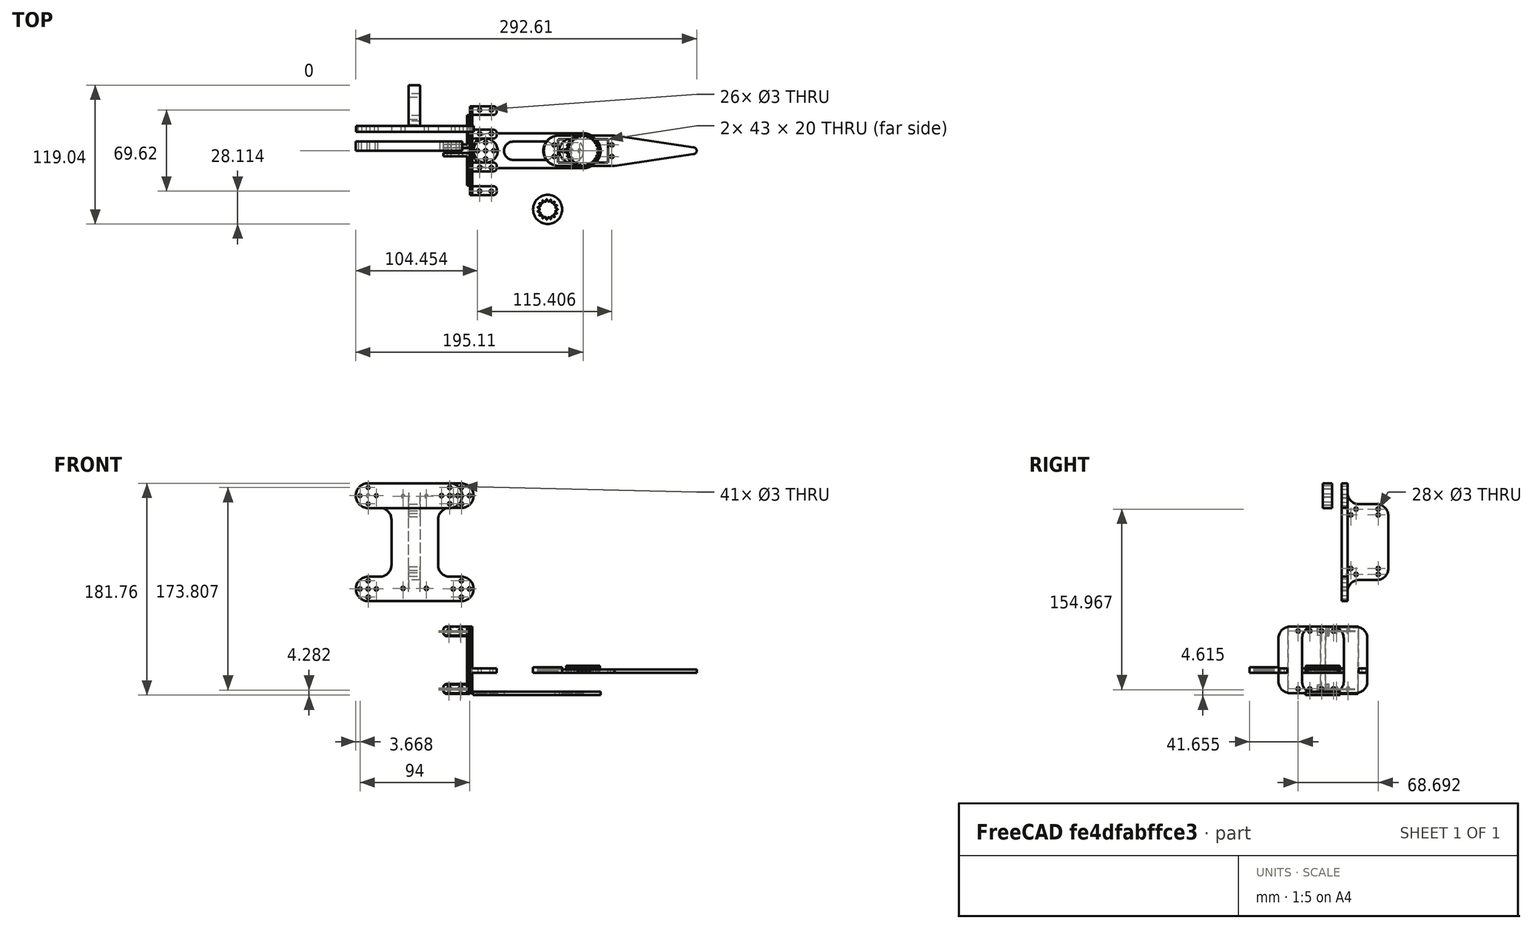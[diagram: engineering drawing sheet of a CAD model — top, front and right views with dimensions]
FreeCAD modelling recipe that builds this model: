
FCSTD DOCUMENT  (FreeCAD 0.21R33771 (Git))
Label: Quadrupedal Robot
License: All rights reserved
LicenseURL: https://en.wikipedia.org/wiki/All_rights_reserved
objects: Sketcher::SketchObject×60, PartDesign::Pocket×33, Mesh::Feature×29, PartDesign::Pad×27, PartDesign::Body×18, App::LinkGroup×18, PartDesign::Fillet×17, App::DocumentObjectGroup×7, Part::Part2DObjectPython×4, App::MeasureDistance×3, Part::FeaturePython×3
note: 239 computed .brp shape members not serialized (recipe doc carries the construction recipe); baked Part::Feature solids carry a one-line shape summary decoded from their .brp

FEATURE [Sketcher::SketchObject] Sketch011
  FullyConstrained = false
  MapMode = 5
  Support = -> [XY_Plane001]
  sketch-geometry (18):
    g0: ArcOfCircle CenterX=-79.4439 CenterY=0 CenterZ=0 NormalX=0 NormalY=0 NormalZ=1 AngleXU=0 Radius=15 StartAngle=1.5708 EndAngle=4.71239
    g1: ArcOfCircle CenterX=0 CenterY=0 CenterZ=0 NormalX=0 NormalY=0 NormalZ=1 AngleXU=0 Radius=15 StartAngle=4.71239 EndAngle=7.85398
    g2: LineSegment StartX=-79.4439 StartY=-15 StartZ=0 EndX=0 EndY=-15 EndZ=0
    g3: LineSegment StartX=4.6e-15 StartY=15 StartZ=0 EndX=-79.4439 EndY=15 EndZ=0
    g4: Circle CenterX=-83.6435 CenterY=7.0054 CenterZ=0 NormalX=0 NormalY=0 NormalZ=1 AngleXU=0 Radius=1.5
    g5: Circle CenterX=-76.656 CenterY=0 CenterZ=0 NormalX=0 NormalY=0 NormalZ=1 AngleXU=0 Radius=1.5
    g6: Circle CenterX=-90.656 CenterY=0 CenterZ=0 NormalX=0 NormalY=0 NormalZ=1 AngleXU=0 Radius=1.5
    g7: Circle CenterX=-83.6435 CenterY=-6.9946 CenterZ=0 NormalX=0 NormalY=0 NormalZ=1 AngleXU=0 Radius=1.5
    g8: Circle CenterX=-9.95164 CenterY=6.96376 CenterZ=0 NormalX=0 NormalY=0 NormalZ=1 AngleXU=0 Radius=1.5
    g9: Circle CenterX=-2.96346 CenterY=0 CenterZ=0 NormalX=0 NormalY=0 NormalZ=1 AngleXU=0 Radius=1.5
    g10: Circle CenterX=-16.9635 CenterY=0 CenterZ=0 NormalX=0 NormalY=0 NormalZ=1 AngleXU=0 Radius=1.5
    g11: Circle CenterX=-9.95164 CenterY=-7.03624 CenterZ=0 NormalX=0 NormalY=0 NormalZ=1 AngleXU=0 Radius=1.5
    g12: ArcOfCircle CenterX=-60.0538 CenterY=0 CenterZ=0 NormalX=0 NormalY=0 NormalZ=1 AngleXU=0 Radius=7.83101 StartAngle=1.5708 EndAngle=4.71239
    g13: ArcOfCircle CenterX=-32.1156 CenterY=0 CenterZ=0 NormalX=0 NormalY=0 NormalZ=1 AngleXU=0 Radius=7.83101 StartAngle=4.71239 EndAngle=7.85398
    g14: LineSegment StartX=-60.0538 StartY=-7.83101 StartZ=0 EndX=-32.1156 EndY=-7.83101 EndZ=0
    g15: LineSegment StartX=-32.1156 StartY=7.83101 StartZ=0 EndX=-60.0538 EndY=7.83101 EndZ=0
    g16: Circle CenterX=-83.6435 CenterY=0 CenterZ=0 NormalX=0 NormalY=0 NormalZ=1 AngleXU=0 Radius=1.5
    g17: Circle CenterX=-9.95164 CenterY=0 CenterZ=0 NormalX=0 NormalY=0 NormalZ=1 AngleXU=0 Radius=1.5
  constraints (44):
    c: Tangent(g0,g2) = -1.5708
    c: Tangent(g2,g1) = -1.5708
    c: Tangent(g1,g3) = -1.5708
    c: Tangent(g3,g0) = -1.5708
    c: Equal(g0,g1)
    c: PointOnObject(g0,g-1)
    c: Coincident(g1,g-1)
    c: Radius(g1) = 15
    c: PointOnObject(g5,g-1)
    c: PointOnObject(g6,g-1)
    c: Equal(g7,g5)
    c: Equal(g5,g4)
    c: Equal(g4,g6)
    c: Diameter(g4) = 3
    c: Vertical(g4,g7)
    c: DistanceX(g6,g5) = 14
    c: DistanceY(g7,g4) = 14
    c: PointOnObject(g9,g-1)
    c: PointOnObject(g10,g-1)
    c: Equal(g11,g10)
    c: Equal(g10,g8)
    c: Equal(g8,g9)
    c: Diameter(g8) = 3
    c: DistanceX(g10,g9) = 14
    c: DistanceY(g11,g8) = 14
    c: Tangent(g12,g14) = -1.5708
    c: Tangent(g14,g13) = -1.5708
    c: Tangent(g13,g15) = -1.5708
    c: Tangent(g15,g12) = -1.5708
    c: Equal(g12,g13)
    c: PointOnObject(g12,g-1)
    c: PointOnObject(g13,g-1)
    c: PointOnObject(g16,g-1)
    c: PointOnObject(g17,g-1)
    c: Equal(g8,g17)
    c: Equal(g16,g5)
    c: Block(g5)
    c: Block(g4)
    c: Vertical(g16,g7)
    c: Block(g8)
    c: Block(g9)
    c: Vertical(g11,g8)
    c: Vertical(g17,g11)
    c: Block(g15)
FEATURE [Sketcher::SketchObject] Sketch013
  AttachmentOffset = pos=(0,0,1) rot=(0,0,1;0rad)
  FullyConstrained = false
  MapMode = 5
  Placement = pos=(0,0,1) rot=(0,0,1;0rad)
  Support = -> [XY_Plane001]
  sketch-geometry (2):
    g0: Circle CenterX=-10 CenterY=0 CenterZ=0 NormalX=0 NormalY=0 NormalZ=1 AngleXU=0 Radius=10.35
    g1: Circle CenterX=-83.6208 CenterY=0 CenterZ=0 NormalX=0 NormalY=0 NormalZ=1 AngleXU=0 Radius=10.35
  constraints (5):
    c: PointOnObject(g0,g-1)
    c: PointOnObject(g1,g-1)
    c: Equal(g1,g0)
    c: Diameter(g0) = 20.7
    c: DistanceX(g0,g-1) = 10
FEATURE [Mesh::Feature] MG997  label="MG995_003"
  Placement = pos=(-148.28,-6.40133,4.14478) rot=(-0.574323,0.579357,-0.578358;4.18879rad)
FEATURE [Mesh::Feature] MG955_horn___Part_1  label="MG955 horn - 002"
  Placement = pos=(-83.66,-0.03,-15.72) rot=(1,0,0;4.71239rad)
FEATURE [Mesh::Feature] MG955_horn___Part_002  label="MG955 horn - 001"
  Placement = pos=(-9.96,-0.03,-15.72) rot=(1,0,0;4.71239rad)
FEATURE [Mesh::Feature] _98zz_Bearing  label="698zz Bearing"
  Placement = pos=(-157.68,6.64,14.25) rot=(1,0,0;4.71239rad)
FEATURE [Sketcher::SketchObject] Sketch024
  AttachmentOffset = pos=(0,0,-0.25) rot=(0,0,1;0rad)
  FullyConstrained = true
  MapMode = 5
  Placement = pos=(0,0.25,1e-16) rot=(1,0,0;1.5708rad)
  Support = -> [XZ_Plane009]
  sketch-geometry (4):
    g0: LineSegment StartX=-99.4442 StartY=39.7122 StartZ=0 EndX=-97.4442 EndY=39.7122 EndZ=0
    g1: LineSegment StartX=-97.4442 StartY=39.7122 StartZ=0 EndX=-97.4442 EndY=-17.2878 EndZ=0
    g2: LineSegment StartX=-97.4442 StartY=-17.2878 StartZ=0 EndX=-99.4442 EndY=-17.2878 EndZ=0
    g3: LineSegment StartX=-99.4442 StartY=-17.2878 StartZ=0 EndX=-99.4442 EndY=39.7122 EndZ=0
  constraints (11):
    c: Coincident(g0,g1)
    c: Coincident(g1,g2)
    c: Coincident(g2,g3)
    c: Coincident(g3,g0)
    c: Horizontal(g0)
    c: Horizontal(g2)
    c: Vertical(g1)
    c: Vertical(g3)
    c: DistanceX(g2,g2) = 2
    c: DistanceY(g3,g3) = 57
    c: Block(g1)
FEATURE [PartDesign::Pad] Pad017
  Direction = (0,-1,2e-16)
  Length = 30
  Length2 = 10
  Placement = pos=(0,0,0) rot=(1,0,0;1.5708rad)
  Profile = -> Sketch024
  ReferenceAxis = -> Sketch024 [N_Axis]
  Type = 0
FEATURE [Sketcher::SketchObject] Sketch025
  AttachmentOffset = pos=(0,0,-98) rot=(0,0,1;0rad)
  ExternalGeometry = -> [Pad017]
  FullyConstrained = true
  MapMode = 5
  Placement = pos=(-98,2.18e-14,-2.18e-14) rot=(0.57735,0.57735,0.57735;2.0944rad)
  Support = -> [YZ_Plane009]
  sketch-geometry (4):
    g0: LineSegment StartX=-4.75 StartY=39.7122 StartZ=0 EndX=-1.75 EndY=39.7122 EndZ=0
    g1: LineSegment StartX=-1.75 StartY=39.7122 StartZ=0 EndX=-1.75 EndY=-17.2878 EndZ=0
    g2: LineSegment StartX=-1.75 StartY=-17.2878 StartZ=0 EndX=-4.75 EndY=-17.2878 EndZ=0
    g3: LineSegment StartX=-4.75 StartY=-17.2878 StartZ=0 EndX=-4.75 EndY=39.7122 EndZ=0
  constraints (12):
    c: Coincident(g0,g1)
    c: Coincident(g1,g2)
    c: Coincident(g2,g3)
    c: Coincident(g3,g0)
    c: Horizontal(g0)
    c: Horizontal(g2)
    c: Vertical(g1)
    c: Vertical(g3)
    c: PointOnObject(g0,g-3)
    c: PointOnObject(g1,g-4)
    c: DistanceX(g0,g0) = 3
    c: DistanceX(g0,g-3) = 2
FEATURE [PartDesign::Pad] Pad018
  BaseFeature = -> Pad017
  Direction = (1,-2e-16,3e-16)
  Length = 22
  Length2 = 10
  Placement = pos=(0,0,0) rot=(1,0,0;1.5708rad)
  Profile = -> Sketch025
  ReferenceAxis = -> Sketch025 [N_Axis]
  Reversed = true
  Type = 0
FEATURE [Sketcher::SketchObject] Sketch026
  AttachmentOffset = pos=(0,0,-156.5) rot=(0,0,1;0rad)
  FullyConstrained = false
  MapMode = 5
  Placement = pos=(-156.5,3.47e-14,-3.47e-14) rot=(0.57735,0.57735,0.57735;2.0944rad)
  Support = -> [YZ_Plane009]
  sketch-geometry (4):
    g0: LineSegment StartX=-30.4604 StartY=32.0705 StartZ=0 EndX=1.50281 EndY=32.0705 EndZ=0
    g1: LineSegment StartX=1.50281 StartY=32.0705 StartZ=0 EndX=1.50281 EndY=-9.92951 EndZ=0
    g2: LineSegment StartX=1.50281 StartY=-9.92951 StartZ=0 EndX=-30.4604 EndY=-9.92951 EndZ=0
    g3: LineSegment StartX=-30.4604 StartY=-9.92951 StartZ=0 EndX=-30.4604 EndY=32.0705 EndZ=0
  constraints (9):
    c: Coincident(g0,g1)
    c: Coincident(g1,g2)
    c: Coincident(g2,g3)
    c: Coincident(g3,g0)
    c: Horizontal(g0)
    c: Horizontal(g2)
    c: Vertical(g1)
    c: Vertical(g3)
    c: DistanceY(g1,g1) = 42
FEATURE [PartDesign::Pocket] Pocket005
  BaseFeature = -> Pad018
  Direction = (-1,2e-16,-3e-16)
  Length = 0
  Length2 = 5
  Placement = pos=(0,0,0) rot=(1,0,0;1.5708rad)
  Profile = -> Sketch026
  ReferenceAxis = -> Sketch026 [N_Axis]
  Type = 3
  UpToFace = -> Pad018 [Face5]
FEATURE [Sketcher::SketchObject] Sketch027
  FullyConstrained = true
  MapMode = 5
  Placement = pos=(0,0,0) rot=(1,0,0;1.5708rad)
  Support = -> [XZ_Plane009]
  sketch-geometry (4):
    g0: Circle CenterX=-114.988 CenterY=36.3647 CenterZ=0 NormalX=0 NormalY=0 NormalZ=1 AngleXU=0 Radius=1.5
    g1: Circle CenterX=-105.112 CenterY=36.3647 CenterZ=0 NormalX=0 NormalY=0 NormalZ=1 AngleXU=0 Radius=1.5
    g2: Circle CenterX=-114.988 CenterY=-13.0424 CenterZ=0 NormalX=0 NormalY=0 NormalZ=1 AngleXU=0 Radius=1.5
    g3: Circle CenterX=-104.988 CenterY=-13.0424 CenterZ=0 NormalX=0 NormalY=0 NormalZ=1 AngleXU=0 Radius=1.5
  constraints (11):
    c: Horizontal(g3,g2)
    c: Horizontal(g0,g1)
    c: Vertical(g0,g2)
    c: Diameter(g1) = 3
    c: Equal(g0,g1)
    c: Equal(g2,g3)
    c: Equal(g3,g1)
    c: DistanceX(g2,g3) = 10
    c: Block(g1)
    c: Block(g0)
    c: Block(g2)
FEATURE [PartDesign::Pocket] Pocket006
  BaseFeature = -> Pocket005
  Direction = (0,1,-2e-16)
  Length = 5
  Length2 = 5
  Placement = pos=(0,0,0) rot=(1,0,0;1.5708rad)
  Profile = -> Sketch027
  ReferenceAxis = -> Sketch027 [N_Axis]
  Reversed = true
  Type = 1
FEATURE [Sketcher::SketchObject] Sketch028
  AttachmentOffset = pos=(0,0,-18) rot=(0,0,1;0rad)
  FullyConstrained = true
  MapMode = 5
  Placement = pos=(0,18,4e-15) rot=(1,0,0;1.5708rad)
  Support = -> [XZ_Plane010]
  sketch-geometry (4):
    g0: LineSegment StartX=-97.0237 StartY=39.7039 StartZ=0 EndX=-95.0237 EndY=39.7039 EndZ=0
    g1: LineSegment StartX=-95.0237 StartY=39.7039 StartZ=0 EndX=-95.0237 EndY=-17.2961 EndZ=0
    g2: LineSegment StartX=-95.0237 StartY=-17.2961 StartZ=0 EndX=-97.0237 EndY=-17.2961 EndZ=0
    g3: LineSegment StartX=-97.0237 StartY=-17.2961 StartZ=0 EndX=-97.0237 EndY=39.7039 EndZ=0
  constraints (11):
    c: Coincident(g0,g1)
    c: Coincident(g1,g2)
    c: Coincident(g3,g0)
    c: Horizontal(g0)
    c: Horizontal(g2)
    c: Vertical(g1)
    c: Vertical(g3)
    c: DistanceX(g0,g0) = 2
    c: Coincident(g3,g2)
    c: DistanceY(g1,g1) = 57
    c: Block(g1)
FEATURE [PartDesign::Pad] Pad019
  Direction = (0,-1,2e-16)
  Length = 56
  Length2 = 10
  Placement = pos=(0,0,0) rot=(1,0,0;1.5708rad)
  Profile = -> Sketch028
  ReferenceAxis = -> Sketch028 [N_Axis]
  Type = 0
FEATURE [Sketcher::SketchObject] Sketch029
  AttachmentOffset = pos=(0,0,-74) rot=(0,0,1;0rad)
  ExternalGeometry = -> [Pad019]
  FullyConstrained = true
  MapMode = 5
  Placement = pos=(-74,1.64e-14,-1.64e-14) rot=(0.57735,0.57735,0.57735;2.0944rad)
  Support = -> [YZ_Plane010]
  sketch-geometry (4):
    g0: LineSegment StartX=-38 StartY=0 StartZ=0 EndX=18 EndY=0 EndZ=0
    g1: LineSegment StartX=18 StartY=0 StartZ=0 EndX=18 EndY=4 EndZ=0
    g2: LineSegment StartX=18 StartY=4 StartZ=0 EndX=-38 EndY=4 EndZ=0
    g3: LineSegment StartX=-38 StartY=4 StartZ=0 EndX=-38 EndY=0 EndZ=0
  constraints (12):
    c: Coincident(g0,g1)
    c: Coincident(g1,g2)
    c: Coincident(g2,g3)
    c: Coincident(g3,g0)
    c: Horizontal(g0)
    c: Horizontal(g2)
    c: Vertical(g1)
    c: Vertical(g3)
    c: PointOnObject(g0,g-3)
    c: PointOnObject(g1,g-4)
    c: PointOnObject(g0,g-1)
    c: DistanceY(g1,g1) = 4
FEATURE [PartDesign::Pad] Pad020
  BaseFeature = -> Pad019
  Direction = (1,-2e-16,3e-16)
  Length = 10
  Length2 = 10
  Placement = pos=(0,0,0) rot=(1,0,0;1.5708rad)
  Profile = -> Sketch029
  ReferenceAxis = -> Sketch029 [N_Axis]
  Type = 3
  UpToFace = -> Pad019 [Face2]
FEATURE [Sketcher::SketchObject] Sketch030
  FullyConstrained = false
  MapMode = 5
  Placement = pos=(0,0,0) rot=(0.57735,0.57735,0.57735;2.0944rad)
  Support = -> [YZ_Plane010]
  sketch-geometry (4):
    g0: LineSegment StartX=-30.4465 StartY=4.63736 StartZ=0 EndX=10.5535 EndY=4.63736 EndZ=0
    g1: LineSegment StartX=10.5535 StartY=4.63736 StartZ=0 EndX=10.5535 EndY=-3.9404 EndZ=0
    g2: LineSegment StartX=10.5535 StartY=-3.9404 StartZ=0 EndX=-30.4465 EndY=-3.9404 EndZ=0
    g3: LineSegment StartX=-30.4465 StartY=-3.9404 StartZ=0 EndX=-30.4465 EndY=4.63736 EndZ=0
  constraints (9):
    c: Coincident(g0,g1)
    c: Coincident(g1,g2)
    c: Coincident(g2,g3)
    c: Coincident(g3,g0)
    c: Horizontal(g0)
    c: Horizontal(g2)
    c: Vertical(g1)
    c: Vertical(g3)
    c: DistanceX(g0,g0) = 41
FEATURE [PartDesign::Pocket] Pocket007
  BaseFeature = -> Pad020
  Direction = (-1,2e-16,-3e-16)
  Length = 0
  Length2 = 5
  Placement = pos=(0,0,0) rot=(1,0,0;1.5708rad)
  Profile = -> Sketch030
  ReferenceAxis = -> Sketch030 [N_Axis]
  Type = 3
  UpToFace = -> Pad020 [Face9]
FEATURE [Sketcher::SketchObject] Sketch031
  FullyConstrained = true
  MapMode = 5
  Support = -> [XY_Plane010]
  sketch-geometry (4):
    g0: Circle CenterX=-88.7181 CenterY=14.6635 CenterZ=0 NormalX=0 NormalY=0 NormalZ=1 AngleXU=0 Radius=1.5
    g1: Circle CenterX=-78.7181 CenterY=14.6635 CenterZ=0 NormalX=0 NormalY=0 NormalZ=1 AngleXU=0 Radius=1.5
    g2: Circle CenterX=-88.7181 CenterY=-34.6965 CenterZ=0 NormalX=0 NormalY=0 NormalZ=1 AngleXU=0 Radius=1.5
    g3: Circle CenterX=-78.7181 CenterY=-34.6965 CenterZ=0 NormalX=0 NormalY=0 NormalZ=1 AngleXU=0 Radius=1.5
  constraints (11):
    c: Equal(g3,g2)
    c: Equal(g3,g1)
    c: Equal(g3,g0)
    c: Diameter(g3) = 3
    c: Horizontal(g0,g1)
    c: DistanceX(g0,g1) = 10
    c: Horizontal(g2,g3)
    c: DistanceX(g2,g3) = 10
    c: Vertical(g2,g0)
    c: Block(g1)
    c: Block(g2)
FEATURE [PartDesign::Pocket] Pocket008
  BaseFeature = -> Pocket007
  Direction = (0,0,-1)
  Length = 5
  Length2 = 5
  Placement = pos=(0,0,0) rot=(1,0,0;1.5708rad)
  Profile = -> Sketch031
  ReferenceAxis = -> Sketch031 [N_Axis]
  Reversed = true
  Type = 1
FEATURE [Sketcher::SketchObject] Sketch032
  AttachmentOffset = pos=(0,0,-1) rot=(0,0,1;0rad)
  FullyConstrained = false
  MapMode = 5
  Placement = pos=(0,1,2e-16) rot=(1,0,0;1.5708rad)
  Support = -> [XZ_Plane009]
  sketch-geometry (4):
    g0: LineSegment StartX=-101.574 StartY=41.4203 StartZ=0 EndX=-97.0564 EndY=41.4203 EndZ=0
    g1: LineSegment StartX=-97.0564 StartY=41.4203 StartZ=0 EndX=-97.0564 EndY=-19.084 EndZ=0
    g2: LineSegment StartX=-97.0564 StartY=-19.084 StartZ=0 EndX=-101.574 EndY=-19.084 EndZ=0
    g3: LineSegment StartX=-101.574 StartY=-19.084 StartZ=0 EndX=-101.574 EndY=41.4203 EndZ=0
  constraints (8):
    c: Coincident(g0,g1)
    c: Coincident(g1,g2)
    c: Coincident(g2,g3)
    c: Coincident(g3,g0)
    c: Horizontal(g0)
    c: Horizontal(g2)
    c: Vertical(g1)
    c: Vertical(g3)
FEATURE [PartDesign::Pocket] Pocket009
  BaseFeature = -> Pocket006
  Direction = (0,1,-2e-16)
  Length = 0
  Length2 = 5
  Placement = pos=(0,0,0) rot=(1,0,0;1.5708rad)
  Profile = -> Sketch032
  ReferenceAxis = -> Sketch032 [N_Axis]
  Reversed = true
  Type = 3
  UpToFace = -> Pocket006 [Face17]
FEATURE [PartDesign::Fillet] Fillet006
  Base = -> Pocket009 [Edge57,Edge63,Edge36,Edge51]
  BaseFeature = -> Pocket009
  Placement = pos=(0,0,0) rot=(1,0,0;1.5708rad)
  Radius = 3
  SupportTransform = false
  UseAllEdges = false
FEATURE [Sketcher::SketchObject] Sketch033
  FullyConstrained = false
  MapMode = 5
  Placement = pos=(0,0,0) rot=(0.57735,0.57735,0.57735;2.0944rad)
  Support = -> [YZ_Plane010]
  sketch-geometry (4):
    g0: Circle CenterX=-11.1549 CenterY=35.9602 CenterZ=0 NormalX=0 NormalY=0 NormalZ=1 AngleXU=0 Radius=1.5
    g1: Circle CenterX=-21.1549 CenterY=35.9602 CenterZ=0 NormalX=0 NormalY=0 NormalZ=1 AngleXU=0 Radius=1.5
    g2: Circle CenterX=-11.1549 CenterY=-13.701 CenterZ=0 NormalX=0 NormalY=0 NormalZ=1 AngleXU=0 Radius=1.5
    g3: Circle CenterX=-21.1549 CenterY=-13.701 CenterZ=0 NormalX=0 NormalY=0 NormalZ=1 AngleXU=0 Radius=1.5
  constraints (9):
    c: Equal(g0,g1)
    c: Diameter(g0) = 3
    c: DistanceX(g1,g0) = 10
    c: Horizontal(g0,g1)
    c: Equal(g3,g2)
    c: Diameter(g3) = 3
    c: Horizontal(g2,g3)
    c: DistanceX(g3,g2) = 10
    c: Vertical(g2,g0)
FEATURE [PartDesign::Pocket] Pocket010
  BaseFeature = -> Pocket008
  Direction = (-1,2e-16,-3e-16)
  Length = 0
  Length2 = 5
  Placement = pos=(0,0,0) rot=(1,0,0;1.5708rad)
  Profile = -> Sketch033
  ReferenceAxis = -> Sketch033 [N_Axis]
  Reversed = true
  Type = 3
  UpToFace = -> Fillet006 [Face4]
FEATURE [Sketcher::SketchObject] Sketch034
  FullyConstrained = true
  MapMode = 5
  Placement = pos=(0,0,0) rot=(0.57735,0.57735,0.57735;2.0944rad)
  Support = -> [YZ_Plane009]
  sketch-geometry (4):
    g0: Circle CenterX=-21.1481 CenterY=35.969 CenterZ=0 NormalX=0 NormalY=0 NormalZ=1 AngleXU=0 Radius=1.5
    g1: Circle CenterX=-11.1481 CenterY=35.969 CenterZ=0 NormalX=0 NormalY=0 NormalZ=1 AngleXU=0 Radius=1.5
    g2: Circle CenterX=-21.1481 CenterY=-13.7095 CenterZ=0 NormalX=0 NormalY=0 NormalZ=1 AngleXU=0 Radius=1.5
    g3: Circle CenterX=-11.1481 CenterY=-13.7095 CenterZ=0 NormalX=0 NormalY=0 NormalZ=1 AngleXU=0 Radius=1.5
  constraints (11):
    c: Equal(g3,g2)
    c: Equal(g3,g0)
    c: Equal(g3,g1)
    c: Diameter(g3) = 3
    c: Horizontal(g0,g1)
    c: DistanceX(g0,g1) = 10
    c: Horizontal(g2,g3)
    c: DistanceX(g2,g3) = 10
    c: Vertical(g2,g0)
    c: Block(g1)
    c: Block(g2)
FEATURE [PartDesign::Pocket] Pocket011
  BaseFeature = -> Fillet006
  Direction = (-1,2e-16,-3e-16)
  Length = 0
  Length2 = 5
  Placement = pos=(0,0,0) rot=(1,0,0;1.5708rad)
  Profile = -> Sketch034
  ReferenceAxis = -> Sketch034 [N_Axis]
  Type = 3
  UpToFace = -> Fillet006 [Face4]
FEATURE [PartDesign::Body] Body009  label="coxa_1"
  Group = -> [Sketch024,Pad017,Sketch025,Pad018,Sketch026,Pocket005,Sketch027,Pocket006,Sketch032,Pocket009,Fillet006,Sketch034,Pocket011]
  Origin = -> Origin009
  Tip = -> Pocket011
FEATURE [PartDesign::Fillet] Fillet007
  Base = -> Pocket010 [Edge64,Edge52,Edge54,Edge45]
  BaseFeature = -> Pocket010
  Placement = pos=(0,0,0) rot=(1,0,0;1.5708rad)
  Radius = 3
  SupportTransform = false
  UseAllEdges = false
FEATURE [PartDesign::Fillet] Fillet008
  Base = -> Fillet007 [Edge36,Edge34,Edge45,Edge42]
  BaseFeature = -> Fillet007
  Placement = pos=(0,0,0) rot=(1,0,0;1.5708rad)
  Radius = 10
  SupportTransform = false
  UseAllEdges = false
FEATURE [PartDesign::Body] Body010  label="coxa_2"
  Group = -> [Sketch028,Pad019,Sketch029,Pad020,Sketch030,Pocket007,Sketch031,Pocket008,Sketch033,Pocket010,Fillet007,Fillet008]
  Origin = -> Origin010
  Tip = -> Fillet008
FEATURE [Mesh::Feature] MG955_horn___Part_004  label="MG955 horn - 004"
  Placement = pos=(-148.18,9.46278,-5.87693) rot=(-1,0,0;6.28144rad)
FEATURE [Mesh::Feature] MG998  label="MG995_004"
  Placement = pos=(-148.28,-6.40133,4.14478) rot=(-0.574323,0.579357,-0.578358;4.18879rad)
FEATURE [Mesh::Feature] MG995  label="MG995_001"
FEATURE [App::LinkGroup] LinkGroup003  label="001"
  ElementList = -> [MG955_horn___Part_002,MG995]
  LinkMode = 0
FEATURE [App::LinkGroup] LinkGroup001  label="004"
  ElementList = -> [MG955_horn___Part_004,MG998]
  LinkMode = 0
  Placement = pos=(-34.2,4.66,7.39) rot=(0,0,1;0rad)
FEATURE [App::DocumentObjectGroup] Group003  label="coxa"
  Group = -> [Body009,Body010]
FEATURE [Sketcher::SketchObject] Sketch023
  FullyConstrained = false
  MapMode = 5
  Support = -> [XY_Plane008]
  sketch-geometry (13):
    g0: LineSegment StartX=-21.5 StartY=-10 StartZ=0 EndX=21.5 EndY=-10 EndZ=0
    g1: LineSegment StartX=21.5 StartY=-10 StartZ=0 EndX=21.5 EndY=10 EndZ=0
    g2: LineSegment StartX=21.5 StartY=10 StartZ=0 EndX=-21.5 EndY=10 EndZ=0
    g3: LineSegment StartX=-21.5 StartY=10 StartZ=0 EndX=-21.5 EndY=-10 EndZ=0
    g4: Circle CenterX=-24.75 CenterY=-5 CenterZ=0 NormalX=0 NormalY=0 NormalZ=1 AngleXU=0 Radius=1.5
    g5: Circle CenterX=-24.75 CenterY=5 CenterZ=0 NormalX=0 NormalY=0 NormalZ=1 AngleXU=0 Radius=1.5
    g6: Circle CenterX=24.75 CenterY=-5 CenterZ=0 NormalX=0 NormalY=0 NormalZ=1 AngleXU=0 Radius=1.5
    g7: Circle CenterX=24.75 CenterY=5 CenterZ=0 NormalX=0 NormalY=0 NormalZ=1 AngleXU=0 Radius=1.5
    g8: LineSegment StartX=27.1868 StartY=-13 StartZ=0 EndX=-21.0434 EndY=-13 EndZ=0
    g9: ArcOfCircle CenterX=-21.0434 CenterY=-2e-16 CenterZ=0 NormalX=0 NormalY=0 NormalZ=1 AngleXU=0 Radius=13 StartAngle=1.5708 EndAngle=4.71239
    g10: LineSegment StartX=-21.0434 StartY=13 StartZ=0 EndX=27.1868 EndY=13 EndZ=0
    g11: LineSegment StartX=27.1868 StartY=13 StartZ=0 EndX=114.981 EndY=1.8e-15 EndZ=0
    g12: LineSegment StartX=27.1868 StartY=-13 StartZ=0 EndX=114.981 EndY=1.8e-15 EndZ=0
  constraints (31):
    c: Coincident(g0,g1)
    c: Coincident(g1,g2)
    c: Coincident(g2,g3)
    c: Coincident(g3,g0)
    c: Horizontal(g0)
    c: Vertical(g1)
    c: Vertical(g3)
    c: DistanceY(g1,g1) = 20
    c: DistanceX(g0,g0) = 43
    c: DistanceY(g0,g-1) = 10
    c: Horizontal(g5,g7)
    c: Horizontal(g4,g6)
    c: Vertical(g6,g7)
    c: Equal(g7,g6)
    c: Equal(g6,g4)
    c: Equal(g4,g5)
    c: Diameter(g6) = 3
    c: Vertical(g5,g4)
    c: DistanceY(g4,g5) = 10
    c: Symmetric(g2,g1,g-2)
    c: Horizontal(g8)
    c: DistanceY(g8,g0) = 3
    c: Coincident(g9,g8)
    c: DistanceY(g2,g9) = 3
    c: Coincident(g10,g9)
    c: Horizontal(g10)
    c: Equal(g10,g8)
    c: Coincident(g11,g10)
    c: PointOnObject(g11,g-1)
    c: Coincident(g12,g8)
    c: Coincident(g12,g11)
FEATURE [PartDesign::Pad] Pad016
  Direction = (0,0,1)
  Length = 3
  Length2 = 10
  Profile = -> Sketch023
  ReferenceAxis = -> Sketch023 [N_Axis]
  Type = 0
FEATURE [PartDesign::Fillet] Fillet005
  Base = -> Pad016 [Edge11]
  BaseFeature = -> Pad016
  Radius = 3
  SupportTransform = false
  UseAllEdges = false
FEATURE [PartDesign::Body] Body008  label="tibia001"
  Group = -> [Sketch023,Pad016,Fillet005]
  Origin = -> Origin008
  Tip = -> Fillet005
FEATURE [App::DocumentObjectGroup] Group004  label="tibia"
  Group = -> [Body008]
FEATURE [Mesh::Feature] MG955_horn___Part_005  label="MG955 horn - 005"
  Placement = pos=(-9.96,-0.03,-15.72) rot=(1,0,0;4.71239rad)
FEATURE [Mesh::Feature] MG955_horn___Part_006  label="MG955 horn - 006"
  Placement = pos=(-148.18,9.46278,-5.87693) rot=(-1,0,0;6.28144rad)
FEATURE [Mesh::Feature] MG955_horn___Part_007  label="MG955 horn - 007"
  Placement = pos=(-83.66,-0.03,-15.72) rot=(1,0,0;4.71239rad)
FEATURE [Mesh::Feature] MG999  label="MG995_005"
FEATURE [App::LinkGroup] LinkGroup007  label="001001"
  ElementList = -> [MG955_horn___Part_005,MG999]
  LinkMode = 0
FEATURE [Mesh::Feature] MG1000  label="MG995_006"
  Placement = pos=(-83.7023,-10.014,0) rot=(0,0,-1;1.57429rad)
FEATURE [App::LinkGroup] LinkGroup008  label="002001"
  ElementList = -> [MG955_horn___Part_007,MG1000]
  LinkMode = 0
FEATURE [Mesh::Feature] MG1001  label="MG995_007"
  Placement = pos=(-148.28,-6.40133,4.14478) rot=(-0.004069,-0.706479,0.707723;3.1448rad)
FEATURE [App::LinkGroup] LinkGroup006  label="003001"
  ElementList = -> [MG955_horn___Part_006,MG1001]
  LinkMode = 0
  Placement = pos=(38.3274,4.65999,6.35469) rot=(0,1,0;0.006981rad)
FEATURE [Sketcher::SketchObject] Sketch035
  FullyConstrained = false
  MapMode = 5
  Support = -> [XY_Plane011]
  sketch-geometry (18):
    g0: ArcOfCircle CenterX=-79.4439 CenterY=0 CenterZ=0 NormalX=0 NormalY=0 NormalZ=1 AngleXU=0 Radius=15 StartAngle=1.5708 EndAngle=4.71239
    g1: ArcOfCircle CenterX=0 CenterY=0 CenterZ=0 NormalX=0 NormalY=0 NormalZ=1 AngleXU=0 Radius=15 StartAngle=4.71239 EndAngle=7.85398
    g2: LineSegment StartX=-79.4439 StartY=-15 StartZ=0 EndX=0 EndY=-15 EndZ=0
    g3: LineSegment StartX=4.6e-15 StartY=15 StartZ=0 EndX=-79.4439 EndY=15 EndZ=0
    g4: Circle CenterX=-83.6435 CenterY=7.0054 CenterZ=0 NormalX=0 NormalY=0 NormalZ=1 AngleXU=0 Radius=1.5
    g5: Circle CenterX=-76.656 CenterY=0 CenterZ=0 NormalX=0 NormalY=0 NormalZ=1 AngleXU=0 Radius=1.5
    g6: Circle CenterX=-90.656 CenterY=0 CenterZ=0 NormalX=0 NormalY=0 NormalZ=1 AngleXU=0 Radius=1.5
    g7: Circle CenterX=-83.6435 CenterY=-6.9946 CenterZ=0 NormalX=0 NormalY=0 NormalZ=1 AngleXU=0 Radius=1.5
    g8: Circle CenterX=-9.95164 CenterY=6.96376 CenterZ=0 NormalX=0 NormalY=0 NormalZ=1 AngleXU=0 Radius=1.5
    g9: Circle CenterX=-2.96346 CenterY=0 CenterZ=0 NormalX=0 NormalY=0 NormalZ=1 AngleXU=0 Radius=1.5
    g10: Circle CenterX=-16.9635 CenterY=0 CenterZ=0 NormalX=0 NormalY=0 NormalZ=1 AngleXU=0 Radius=1.5
    g11: Circle CenterX=-9.95164 CenterY=-7.03624 CenterZ=0 NormalX=0 NormalY=0 NormalZ=1 AngleXU=0 Radius=1.5
    g12: ArcOfCircle CenterX=-60.0538 CenterY=0 CenterZ=0 NormalX=0 NormalY=0 NormalZ=1 AngleXU=0 Radius=7.83101 StartAngle=1.5708 EndAngle=4.71239
    g13: ArcOfCircle CenterX=-32.1156 CenterY=0 CenterZ=0 NormalX=0 NormalY=0 NormalZ=1 AngleXU=0 Radius=7.83101 StartAngle=4.71239 EndAngle=7.85398
    g14: LineSegment StartX=-60.0538 StartY=-7.83101 StartZ=0 EndX=-32.1156 EndY=-7.83101 EndZ=0
    g15: LineSegment StartX=-32.1156 StartY=7.83101 StartZ=0 EndX=-60.0538 EndY=7.83101 EndZ=0
    g16: Circle CenterX=-83.6435 CenterY=0 CenterZ=0 NormalX=0 NormalY=0 NormalZ=1 AngleXU=0 Radius=1.5
    g17: Circle CenterX=-9.95164 CenterY=0 CenterZ=0 NormalX=0 NormalY=0 NormalZ=1 AngleXU=0 Radius=1.5
  constraints (44):
    c: Tangent(g0,g2) = -1.5708
    c: Tangent(g2,g1) = -1.5708
    c: Tangent(g1,g3) = -1.5708
    c: Tangent(g3,g0) = -1.5708
    c: Equal(g0,g1)
    c: PointOnObject(g0,g-1)
    c: Coincident(g1,g-1)
    c: Radius(g1) = 15
    c: PointOnObject(g5,g-1)
    c: PointOnObject(g6,g-1)
    c: Equal(g7,g5)
    c: Equal(g5,g4)
    c: Equal(g4,g6)
    c: Diameter(g4) = 3
    c: Vertical(g4,g7)
    c: DistanceX(g6,g5) = 14
    c: DistanceY(g7,g4) = 14
    c: PointOnObject(g9,g-1)
    c: PointOnObject(g10,g-1)
    c: Equal(g11,g10)
    c: Equal(g10,g8)
    c: Equal(g8,g9)
    c: Diameter(g8) = 3
    c: DistanceX(g10,g9) = 14
    c: DistanceY(g11,g8) = 14
    c: Tangent(g12,g14) = -1.5708
    c: Tangent(g14,g13) = -1.5708
    c: Tangent(g13,g15) = -1.5708
    c: Tangent(g15,g12) = -1.5708
    c: Equal(g12,g13)
    c: PointOnObject(g12,g-1)
    c: PointOnObject(g13,g-1)
    c: PointOnObject(g16,g-1)
    c: PointOnObject(g17,g-1)
    c: Equal(g8,g17)
    c: Equal(g16,g5)
    c: Block(g5)
    c: Block(g4)
    c: Vertical(g16,g7)
    c: Block(g8)
    c: Block(g9)
    c: Vertical(g11,g8)
    c: Vertical(g17,g11)
    c: Block(g15)
FEATURE [PartDesign::Pad] Pad021
  Direction = (0,0,1)
  Length = 3
  Length2 = 10
  Profile = -> Sketch035
  ReferenceAxis = -> Sketch035 [N_Axis]
  Type = 0
FEATURE [Sketcher::SketchObject] Sketch037
  AttachmentOffset = pos=(0,0,1) rot=(0,0,1;0rad)
  FullyConstrained = false
  MapMode = 5
  Placement = pos=(0,0,1) rot=(0,0,1;0rad)
  Support = -> [XY_Plane011]
  sketch-geometry (2):
    g0: Circle CenterX=-10 CenterY=0 CenterZ=0 NormalX=0 NormalY=0 NormalZ=1 AngleXU=0 Radius=10.35
    g1: Circle CenterX=-83.6208 CenterY=0 CenterZ=0 NormalX=0 NormalY=0 NormalZ=1 AngleXU=0 Radius=10.35
  constraints (5):
    c: PointOnObject(g0,g-1)
    c: PointOnObject(g1,g-1)
    c: Equal(g1,g0)
    c: Diameter(g0) = 20.7
    c: DistanceX(g0,g-1) = 10
FEATURE [PartDesign::Pocket] Pocket012
  BaseFeature = -> Pad021
  Direction = (0,0,-1)
  Length = 3
  Length2 = 5
  Profile = -> Sketch037
  ReferenceAxis = -> Sketch037 [N_Axis]
  Reversed = true
  Type = 0
FEATURE [PartDesign::Body] Body011  label="femur_x001"
  Group = -> [Sketch035,Pad021,Sketch037,Pocket012]
  Origin = -> Origin011
  Placement = pos=(0,0,-19) rot=(0,0,1;0rad)
  Tip = -> Pocket012
FEATURE [Sketcher::SketchObject] Sketch038
  FullyConstrained = false
  MapMode = 5
  Support = -> [XY_Plane013]
  sketch-geometry (13):
    g0: LineSegment StartX=-21.5 StartY=-10 StartZ=0 EndX=21.5 EndY=-10 EndZ=0
    g1: LineSegment StartX=21.5 StartY=-10 StartZ=0 EndX=21.5 EndY=10 EndZ=0
    g2: LineSegment StartX=21.5 StartY=10 StartZ=0 EndX=-21.5 EndY=10 EndZ=0
    g3: LineSegment StartX=-21.5 StartY=10 StartZ=0 EndX=-21.5 EndY=-10 EndZ=0
    g4: Circle CenterX=-24.75 CenterY=-5 CenterZ=0 NormalX=0 NormalY=0 NormalZ=1 AngleXU=0 Radius=1.5
    g5: Circle CenterX=-24.75 CenterY=5 CenterZ=0 NormalX=0 NormalY=0 NormalZ=1 AngleXU=0 Radius=1.5
    g6: Circle CenterX=24.75 CenterY=-5 CenterZ=0 NormalX=0 NormalY=0 NormalZ=1 AngleXU=0 Radius=1.5
    g7: Circle CenterX=24.75 CenterY=5 CenterZ=0 NormalX=0 NormalY=0 NormalZ=1 AngleXU=0 Radius=1.5
    g8: LineSegment StartX=27.1868 StartY=-13 StartZ=0 EndX=-20.6907 EndY=-13 EndZ=0
    g9: ArcOfCircle CenterX=-20.6907 CenterY=8e-16 CenterZ=0 NormalX=0 NormalY=0 NormalZ=1 AngleXU=0 Radius=13 StartAngle=1.5708 EndAngle=4.71239
    g10: LineSegment StartX=-20.6907 StartY=13 StartZ=0 EndX=27.1868 EndY=13 EndZ=0
    g11: LineSegment StartX=27.1868 StartY=13 StartZ=0 EndX=114.981 EndY=1.8e-15 EndZ=0
    g12: LineSegment StartX=27.1868 StartY=-13 StartZ=0 EndX=114.981 EndY=1.8e-15 EndZ=0
  constraints (31):
    c: Coincident(g0,g1)
    c: Coincident(g1,g2)
    c: Coincident(g2,g3)
    c: Coincident(g3,g0)
    c: Horizontal(g0)
    c: Vertical(g1)
    c: Vertical(g3)
    c: DistanceY(g1,g1) = 20
    c: DistanceX(g0,g0) = 43
    c: DistanceY(g0,g-1) = 10
    c: Horizontal(g5,g7)
    c: Horizontal(g4,g6)
    c: Vertical(g6,g7)
    c: Equal(g7,g6)
    c: Equal(g6,g4)
    c: Equal(g4,g5)
    c: Diameter(g6) = 3
    c: Vertical(g5,g4)
    c: DistanceY(g4,g5) = 10
    c: Symmetric(g2,g1,g-2)
    c: Horizontal(g8)
    c: DistanceY(g8,g0) = 3
    c: Coincident(g9,g8)
    c: DistanceY(g2,g9) = 3
    c: Coincident(g10,g9)
    c: Horizontal(g10)
    c: Equal(g10,g8)
    c: Coincident(g11,g10)
    c: PointOnObject(g11,g-1)
    c: Coincident(g12,g8)
    c: Coincident(g12,g11)
FEATURE [PartDesign::Pad] Pad023
  Direction = (0,0,1)
  Length = 3
  Length2 = 10
  Profile = -> Sketch038
  ReferenceAxis = -> Sketch038 [N_Axis]
  Type = 0
FEATURE [PartDesign::Fillet] Fillet009
  Base = -> Pad023 [Edge11]
  BaseFeature = -> Pad023
  Radius = 3
  SupportTransform = false
  UseAllEdges = false
FEATURE [PartDesign::Body] Body013  label="tibia002"
  Group = -> [Sketch038,Pad023,Fillet009]
  Origin = -> Origin013
  Tip = -> Fillet009
FEATURE [Sketcher::SketchObject] Sketch039
  AttachmentOffset = pos=(0,0,-0.25) rot=(0,0,1;0rad)
  FullyConstrained = true
  MapMode = 5
  Placement = pos=(0,0.25,1e-16) rot=(1,0,0;1.5708rad)
  Support = -> [XZ_Plane014]
  sketch-geometry (4):
    g0: LineSegment StartX=-99.4442 StartY=39.7122 StartZ=0 EndX=-97.4442 EndY=39.7122 EndZ=0
    g1: LineSegment StartX=-97.4442 StartY=39.7122 StartZ=0 EndX=-97.4442 EndY=-17.2878 EndZ=0
    g2: LineSegment StartX=-97.4442 StartY=-17.2878 StartZ=0 EndX=-99.4442 EndY=-17.2878 EndZ=0
    g3: LineSegment StartX=-99.4442 StartY=-17.2878 StartZ=0 EndX=-99.4442 EndY=39.7122 EndZ=0
  constraints (11):
    c: Coincident(g0,g1)
    c: Coincident(g1,g2)
    c: Coincident(g2,g3)
    c: Coincident(g3,g0)
    c: Horizontal(g0)
    c: Horizontal(g2)
    c: Vertical(g1)
    c: Vertical(g3)
    c: DistanceX(g2,g2) = 2
    c: DistanceY(g3,g3) = 57
    c: Block(g1)
FEATURE [PartDesign::Pad] Pad024
  Direction = (0,-1,2e-16)
  Length = 30
  Length2 = 10
  Placement = pos=(0,0,0) rot=(1,0,0;1.5708rad)
  Profile = -> Sketch039
  ReferenceAxis = -> Sketch039 [N_Axis]
  Type = 0
FEATURE [Sketcher::SketchObject] Sketch040
  AttachmentOffset = pos=(0,0,-98) rot=(0,0,1;0rad)
  ExternalGeometry = -> [Pad024]
  FullyConstrained = true
  MapMode = 5
  Placement = pos=(-98,2.18e-14,-2.18e-14) rot=(0.57735,0.57735,0.57735;2.0944rad)
  Support = -> [YZ_Plane014]
  sketch-geometry (4):
    g0: LineSegment StartX=-4.75 StartY=39.7122 StartZ=0 EndX=-1.75 EndY=39.7122 EndZ=0
    g1: LineSegment StartX=-1.75 StartY=39.7122 StartZ=0 EndX=-1.75 EndY=-17.2878 EndZ=0
    g2: LineSegment StartX=-1.75 StartY=-17.2878 StartZ=0 EndX=-4.75 EndY=-17.2878 EndZ=0
    g3: LineSegment StartX=-4.75 StartY=-17.2878 StartZ=0 EndX=-4.75 EndY=39.7122 EndZ=0
  constraints (12):
    c: Coincident(g0,g1)
    c: Coincident(g1,g2)
    c: Coincident(g2,g3)
    c: Coincident(g3,g0)
    c: Horizontal(g0)
    c: Horizontal(g2)
    c: Vertical(g1)
    c: Vertical(g3)
    c: PointOnObject(g0,g-3)
    c: PointOnObject(g1,g-4)
    c: DistanceX(g0,g0) = 3
    c: DistanceX(g0,g-3) = 2
FEATURE [PartDesign::Pad] Pad025
  BaseFeature = -> Pad024
  Direction = (1,-2e-16,3e-16)
  Length = 22
  Length2 = 10
  Placement = pos=(0,0,0) rot=(1,0,0;1.5708rad)
  Profile = -> Sketch040
  ReferenceAxis = -> Sketch040 [N_Axis]
  Reversed = true
  Type = 0
FEATURE [Sketcher::SketchObject] Sketch041
  AttachmentOffset = pos=(0,0,-156.5) rot=(0,0,1;0rad)
  FullyConstrained = false
  MapMode = 5
  Placement = pos=(-156.5,3.47e-14,-3.47e-14) rot=(0.57735,0.57735,0.57735;2.0944rad)
  Support = -> [YZ_Plane014]
  sketch-geometry (4):
    g0: LineSegment StartX=-30.4604 StartY=32.0705 StartZ=0 EndX=1.50281 EndY=32.0705 EndZ=0
    g1: LineSegment StartX=1.50281 StartY=32.0705 StartZ=0 EndX=1.50281 EndY=-9.92951 EndZ=0
    g2: LineSegment StartX=1.50281 StartY=-9.92951 StartZ=0 EndX=-30.4604 EndY=-9.92951 EndZ=0
    g3: LineSegment StartX=-30.4604 StartY=-9.92951 StartZ=0 EndX=-30.4604 EndY=32.0705 EndZ=0
  constraints (9):
    c: Coincident(g0,g1)
    c: Coincident(g1,g2)
    c: Coincident(g2,g3)
    c: Coincident(g3,g0)
    c: Horizontal(g0)
    c: Horizontal(g2)
    c: Vertical(g1)
    c: Vertical(g3)
    c: DistanceY(g1,g1) = 42
FEATURE [PartDesign::Pocket] Pocket013
  BaseFeature = -> Pad025
  Direction = (-1,2e-16,-3e-16)
  Length = 0
  Length2 = 5
  Placement = pos=(0,0,0) rot=(1,0,0;1.5708rad)
  Profile = -> Sketch041
  ReferenceAxis = -> Sketch041 [N_Axis]
  Type = 3
  UpToFace = -> Pad025 [Face5]
FEATURE [Sketcher::SketchObject] Sketch042
  FullyConstrained = true
  MapMode = 5
  Placement = pos=(0,0,0) rot=(1,0,0;1.5708rad)
  Support = -> [XZ_Plane014]
  sketch-geometry (4):
    g0: Circle CenterX=-114.988 CenterY=36.3647 CenterZ=0 NormalX=0 NormalY=0 NormalZ=1 AngleXU=0 Radius=1.5
    g1: Circle CenterX=-105.112 CenterY=36.3647 CenterZ=0 NormalX=0 NormalY=0 NormalZ=1 AngleXU=0 Radius=1.5
    g2: Circle CenterX=-114.988 CenterY=-13.0424 CenterZ=0 NormalX=0 NormalY=0 NormalZ=1 AngleXU=0 Radius=1.5
    g3: Circle CenterX=-104.988 CenterY=-13.0424 CenterZ=0 NormalX=0 NormalY=0 NormalZ=1 AngleXU=0 Radius=1.5
  constraints (11):
    c: Horizontal(g3,g2)
    c: Horizontal(g0,g1)
    c: Vertical(g0,g2)
    c: Diameter(g1) = 3
    c: Equal(g0,g1)
    c: Equal(g2,g3)
    c: Equal(g3,g1)
    c: DistanceX(g2,g3) = 10
    c: Block(g1)
    c: Block(g0)
    c: Block(g2)
FEATURE [PartDesign::Pocket] Pocket014
  BaseFeature = -> Pocket013
  Direction = (0,1,-2e-16)
  Length = 5
  Length2 = 5
  Placement = pos=(0,0,0) rot=(1,0,0;1.5708rad)
  Profile = -> Sketch042
  ReferenceAxis = -> Sketch042 [N_Axis]
  Reversed = true
  Type = 1
FEATURE [Sketcher::SketchObject] Sketch043
  AttachmentOffset = pos=(0,0,-18) rot=(0,0,1;0rad)
  FullyConstrained = true
  MapMode = 5
  Placement = pos=(0,18,4e-15) rot=(1,0,0;1.5708rad)
  Support = -> [XZ_Plane015]
  sketch-geometry (4):
    g0: LineSegment StartX=-97.0237 StartY=39.7039 StartZ=0 EndX=-95.0237 EndY=39.7039 EndZ=0
    g1: LineSegment StartX=-95.0237 StartY=39.7039 StartZ=0 EndX=-95.0237 EndY=-17.2961 EndZ=0
    g2: LineSegment StartX=-95.0237 StartY=-17.2961 StartZ=0 EndX=-97.0237 EndY=-17.2961 EndZ=0
    g3: LineSegment StartX=-97.0237 StartY=-17.2961 StartZ=0 EndX=-97.0237 EndY=39.7039 EndZ=0
  constraints (11):
    c: Coincident(g0,g1)
    c: Coincident(g1,g2)
    c: Coincident(g3,g0)
    c: Horizontal(g0)
    c: Horizontal(g2)
    c: Vertical(g1)
    c: Vertical(g3)
    c: DistanceX(g0,g0) = 2
    c: Coincident(g3,g2)
    c: DistanceY(g1,g1) = 57
    c: Block(g1)
FEATURE [PartDesign::Pad] Pad026
  Direction = (0,-1,2e-16)
  Length = 56
  Length2 = 10
  Placement = pos=(0,0,0) rot=(1,0,0;1.5708rad)
  Profile = -> Sketch043
  ReferenceAxis = -> Sketch043 [N_Axis]
  Type = 0
FEATURE [Sketcher::SketchObject] Sketch044
  AttachmentOffset = pos=(0,0,-74) rot=(0,0,1;0rad)
  ExternalGeometry = -> [Pad026]
  FullyConstrained = true
  MapMode = 5
  Placement = pos=(-74,1.64e-14,-1.64e-14) rot=(0.57735,0.57735,0.57735;2.0944rad)
  Support = -> [YZ_Plane015]
  sketch-geometry (4):
    g0: LineSegment StartX=-38 StartY=0 StartZ=0 EndX=18 EndY=0 EndZ=0
    g1: LineSegment StartX=18 StartY=0 StartZ=0 EndX=18 EndY=4 EndZ=0
    g2: LineSegment StartX=18 StartY=4 StartZ=0 EndX=-38 EndY=4 EndZ=0
    g3: LineSegment StartX=-38 StartY=4 StartZ=0 EndX=-38 EndY=0 EndZ=0
  constraints (12):
    c: Coincident(g0,g1)
    c: Coincident(g1,g2)
    c: Coincident(g2,g3)
    c: Coincident(g3,g0)
    c: Horizontal(g0)
    c: Horizontal(g2)
    c: Vertical(g1)
    c: Vertical(g3)
    c: PointOnObject(g0,g-3)
    c: PointOnObject(g1,g-4)
    c: PointOnObject(g0,g-1)
    c: DistanceY(g1,g1) = 4
FEATURE [PartDesign::Pad] Pad027
  BaseFeature = -> Pad026
  Direction = (1,-2e-16,3e-16)
  Length = 10
  Length2 = 10
  Placement = pos=(0,0,0) rot=(1,0,0;1.5708rad)
  Profile = -> Sketch044
  ReferenceAxis = -> Sketch044 [N_Axis]
  Type = 3
  UpToFace = -> Pad026 [Face2]
FEATURE [Sketcher::SketchObject] Sketch045
  FullyConstrained = false
  MapMode = 5
  Placement = pos=(0,0,0) rot=(0.57735,0.57735,0.57735;2.0944rad)
  Support = -> [YZ_Plane015]
  sketch-geometry (4):
    g0: LineSegment StartX=-30.4465 StartY=4.63736 StartZ=0 EndX=10.5535 EndY=4.63736 EndZ=0
    g1: LineSegment StartX=10.5535 StartY=4.63736 StartZ=0 EndX=10.5535 EndY=-3.9404 EndZ=0
    g2: LineSegment StartX=10.5535 StartY=-3.9404 StartZ=0 EndX=-30.4465 EndY=-3.9404 EndZ=0
    g3: LineSegment StartX=-30.4465 StartY=-3.9404 StartZ=0 EndX=-30.4465 EndY=4.63736 EndZ=0
  constraints (9):
    c: Coincident(g0,g1)
    c: Coincident(g1,g2)
    c: Coincident(g2,g3)
    c: Coincident(g3,g0)
    c: Horizontal(g0)
    c: Horizontal(g2)
    c: Vertical(g1)
    c: Vertical(g3)
    c: DistanceX(g0,g0) = 41
FEATURE [PartDesign::Pocket] Pocket015
  BaseFeature = -> Pad027
  Direction = (-1,2e-16,-3e-16)
  Length = 0
  Length2 = 5
  Placement = pos=(0,0,0) rot=(1,0,0;1.5708rad)
  Profile = -> Sketch045
  ReferenceAxis = -> Sketch045 [N_Axis]
  Type = 3
  UpToFace = -> Pad027 [Face9]
FEATURE [Sketcher::SketchObject] Sketch046
  FullyConstrained = true
  MapMode = 5
  Support = -> [XY_Plane015]
  sketch-geometry (4):
    g0: Circle CenterX=-88.7181 CenterY=14.6635 CenterZ=0 NormalX=0 NormalY=0 NormalZ=1 AngleXU=0 Radius=1.5
    g1: Circle CenterX=-78.7181 CenterY=14.6635 CenterZ=0 NormalX=0 NormalY=0 NormalZ=1 AngleXU=0 Radius=1.5
    g2: Circle CenterX=-88.7181 CenterY=-34.6965 CenterZ=0 NormalX=0 NormalY=0 NormalZ=1 AngleXU=0 Radius=1.5
    g3: Circle CenterX=-78.7181 CenterY=-34.6965 CenterZ=0 NormalX=0 NormalY=0 NormalZ=1 AngleXU=0 Radius=1.5
  constraints (11):
    c: Equal(g3,g2)
    c: Equal(g3,g1)
    c: Equal(g3,g0)
    c: Diameter(g3) = 3
    c: Horizontal(g0,g1)
    c: DistanceX(g0,g1) = 10
    c: Horizontal(g2,g3)
    c: DistanceX(g2,g3) = 10
    c: Vertical(g2,g0)
    c: Block(g1)
    c: Block(g2)
FEATURE [PartDesign::Pocket] Pocket016
  BaseFeature = -> Pocket015
  Direction = (0,0,-1)
  Length = 5
  Length2 = 5
  Placement = pos=(0,0,0) rot=(1,0,0;1.5708rad)
  Profile = -> Sketch046
  ReferenceAxis = -> Sketch046 [N_Axis]
  Reversed = true
  Type = 1
FEATURE [Sketcher::SketchObject] Sketch047
  AttachmentOffset = pos=(0,0,-1) rot=(0,0,1;0rad)
  FullyConstrained = false
  MapMode = 5
  Placement = pos=(0,1,2e-16) rot=(1,0,0;1.5708rad)
  Support = -> [XZ_Plane014]
  sketch-geometry (4):
    g0: LineSegment StartX=-101.574 StartY=41.4203 StartZ=0 EndX=-97.0564 EndY=41.4203 EndZ=0
    g1: LineSegment StartX=-97.0564 StartY=41.4203 StartZ=0 EndX=-97.0564 EndY=-19.084 EndZ=0
    g2: LineSegment StartX=-97.0564 StartY=-19.084 StartZ=0 EndX=-101.574 EndY=-19.084 EndZ=0
    g3: LineSegment StartX=-101.574 StartY=-19.084 StartZ=0 EndX=-101.574 EndY=41.4203 EndZ=0
  constraints (8):
    c: Coincident(g0,g1)
    c: Coincident(g1,g2)
    c: Coincident(g2,g3)
    c: Coincident(g3,g0)
    c: Horizontal(g0)
    c: Horizontal(g2)
    c: Vertical(g1)
    c: Vertical(g3)
FEATURE [PartDesign::Pocket] Pocket017
  BaseFeature = -> Pocket014
  Direction = (0,1,-2e-16)
  Length = 0
  Length2 = 5
  Placement = pos=(0,0,0) rot=(1,0,0;1.5708rad)
  Profile = -> Sketch047
  ReferenceAxis = -> Sketch047 [N_Axis]
  Reversed = true
  Type = 3
  UpToFace = -> Pocket014 [Face17]
FEATURE [PartDesign::Fillet] Fillet010
  Base = -> Pocket017 [Edge57,Edge63,Edge36,Edge51]
  BaseFeature = -> Pocket017
  Placement = pos=(0,0,0) rot=(1,0,0;1.5708rad)
  Radius = 3
  SupportTransform = false
  UseAllEdges = false
FEATURE [Sketcher::SketchObject] Sketch048
  FullyConstrained = false
  MapMode = 5
  Placement = pos=(0,0,0) rot=(0.57735,0.57735,0.57735;2.0944rad)
  Support = -> [YZ_Plane015]
  sketch-geometry (4):
    g0: Circle CenterX=-11.1549 CenterY=35.9602 CenterZ=0 NormalX=0 NormalY=0 NormalZ=1 AngleXU=0 Radius=1.5
    g1: Circle CenterX=-21.1549 CenterY=35.9602 CenterZ=0 NormalX=0 NormalY=0 NormalZ=1 AngleXU=0 Radius=1.5
    g2: Circle CenterX=-11.1549 CenterY=-13.701 CenterZ=0 NormalX=0 NormalY=0 NormalZ=1 AngleXU=0 Radius=1.5
    g3: Circle CenterX=-21.1549 CenterY=-13.701 CenterZ=0 NormalX=0 NormalY=0 NormalZ=1 AngleXU=0 Radius=1.5
  constraints (9):
    c: Equal(g0,g1)
    c: Diameter(g0) = 3
    c: DistanceX(g1,g0) = 10
    c: Horizontal(g0,g1)
    c: Equal(g3,g2)
    c: Diameter(g3) = 3
    c: Horizontal(g2,g3)
    c: DistanceX(g3,g2) = 10
    c: Vertical(g2,g0)
FEATURE [PartDesign::Pocket] Pocket018
  BaseFeature = -> Pocket016
  Direction = (-1,2e-16,-3e-16)
  Length = 0
  Length2 = 5
  Placement = pos=(0,0,0) rot=(1,0,0;1.5708rad)
  Profile = -> Sketch048
  ReferenceAxis = -> Sketch048 [N_Axis]
  Reversed = true
  Type = 3
  UpToFace = -> Fillet010 [Face4]
FEATURE [PartDesign::Fillet] Fillet011
  Base = -> Pocket018 [Edge64,Edge52,Edge54,Edge45]
  BaseFeature = -> Pocket018
  Placement = pos=(0,0,0) rot=(1,0,0;1.5708rad)
  Radius = 3
  SupportTransform = false
  UseAllEdges = false
FEATURE [PartDesign::Fillet] Fillet012
  Base = -> Fillet011 [Edge36,Edge34,Edge45,Edge42]
  BaseFeature = -> Fillet011
  Placement = pos=(0,0,0) rot=(1,0,0;1.5708rad)
  Radius = 10
  SupportTransform = false
  UseAllEdges = false
FEATURE [PartDesign::Body] Body015  label="coxa_004"
  Group = -> [Sketch043,Pad026,Sketch044,Pad027,Sketch045,Pocket015,Sketch046,Pocket016,Sketch048,Pocket018,Fillet011,Fillet012]
  Origin = -> Origin015
  Tip = -> Fillet012
FEATURE [Sketcher::SketchObject] Sketch049
  FullyConstrained = true
  MapMode = 5
  Placement = pos=(0,0,0) rot=(0.57735,0.57735,0.57735;2.0944rad)
  Support = -> [YZ_Plane014]
  sketch-geometry (4):
    g0: Circle CenterX=-21.1481 CenterY=35.969 CenterZ=0 NormalX=0 NormalY=0 NormalZ=1 AngleXU=0 Radius=1.5
    g1: Circle CenterX=-11.1481 CenterY=35.969 CenterZ=0 NormalX=0 NormalY=0 NormalZ=1 AngleXU=0 Radius=1.5
    g2: Circle CenterX=-21.1481 CenterY=-13.7095 CenterZ=0 NormalX=0 NormalY=0 NormalZ=1 AngleXU=0 Radius=1.5
    g3: Circle CenterX=-11.1481 CenterY=-13.7095 CenterZ=0 NormalX=0 NormalY=0 NormalZ=1 AngleXU=0 Radius=1.5
  constraints (11):
    c: Equal(g3,g2)
    c: Equal(g3,g0)
    c: Equal(g3,g1)
    c: Diameter(g3) = 3
    c: Horizontal(g0,g1)
    c: DistanceX(g0,g1) = 10
    c: Horizontal(g2,g3)
    c: DistanceX(g2,g3) = 10
    c: Vertical(g2,g0)
    c: Block(g1)
    c: Block(g2)
FEATURE [PartDesign::Pocket] Pocket019
  BaseFeature = -> Fillet010
  Direction = (-1,2e-16,-3e-16)
  Length = 0
  Length2 = 5
  Placement = pos=(0,0,0) rot=(1,0,0;1.5708rad)
  Profile = -> Sketch049
  ReferenceAxis = -> Sketch049 [N_Axis]
  Type = 3
  UpToFace = -> Fillet010 [Face4]
FEATURE [PartDesign::Body] Body014  label="coxa_003"
  Group = -> [Sketch039,Pad024,Sketch040,Pad025,Sketch041,Pocket013,Sketch042,Pocket014,Sketch047,Pocket017,Fillet010,Sketch049,Pocket019]
  Origin = -> Origin014
  Tip = -> Pocket019
FEATURE [App::LinkGroup] LinkGroup009  label="LegBL"
  ElementList = -> [Body011,LinkGroup008,LinkGroup007,LinkGroup006,Body014,Body015,Body013]
  LinkMode = 0
  Placement = pos=(5.38,-2.38419e-05,150.56) rot=(0,0,1;0rad)
FEATURE [Mesh::Feature] MG996  label="MG995_002"
  Placement = pos=(-83.7023,-10.014,0) rot=(0,0,-1;1.57429rad)
FEATURE [App::LinkGroup] LinkGroup002  label="005"
  ElementList = -> [MG996,MG955_horn___Part_1]
  LinkMode = 0
  Placement = pos=(-134.77,1.62125e-05,4.76837e-07) rot=(0,0,1;0rad)
FEATURE [Mesh::Feature] MG955_horn___Part_008  label="MG955 horn - 003"
  Placement = pos=(-148.18,9.46278,-5.87693) rot=(-1,0,0;6.28144rad)
FEATURE [App::LinkGroup] LinkGroup  label="003"
  ElementList = -> [MG997,MG955_horn___Part_008]
  LinkMode = 0
  Placement = pos=(-258.234,4.65999,16.2152) rot=(0,1,0;3.14508rad)
FEATURE [App::LinkGroup] LinkGroup004  label="002"
  ElementList = -> [MG955_horn___Part_1,MG996]
  LinkMode = 0
FEATURE [App::DocumentObjectGroup] Group002  label="MG955s"
  Group = -> [LinkGroup004,LinkGroup003,LinkGroup,LinkGroup001,LinkGroup002]
FEATURE [Mesh::Feature] MG955_horn___Part_009  label="MG955 horn - 008"
  Placement = pos=(-9.96,-0.03,-15.72) rot=(1,0,0;4.71239rad)
FEATURE [Mesh::Feature] MG955_horn___Part_010  label="MG955 horn - 009"
  Placement = pos=(-148.18,9.46278,-5.87693) rot=(-1,0,0;6.28144rad)
FEATURE [Mesh::Feature] MG955_horn___Part_011  label="MG955 horn - 010"
  Placement = pos=(-83.66,-0.03,-15.72) rot=(1,0,0;4.71239rad)
FEATURE [Mesh::Feature] MG1002  label="MG995_008"
FEATURE [App::LinkGroup] LinkGroup011  label="001002"
  ElementList = -> [MG955_horn___Part_009,MG1002]
  LinkMode = 0
FEATURE [Mesh::Feature] MG1003  label="MG995_009"
  Placement = pos=(-83.7023,-10.014,0) rot=(0,0,-1;1.57429rad)
FEATURE [App::LinkGroup] LinkGroup012  label="002002"
  ElementList = -> [MG955_horn___Part_011,MG1003]
  LinkMode = 0
  Placement = pos=(-167.334,-0.319952,-4.76837e-07) rot=(0,0,1;3.14508rad)
FEATURE [Mesh::Feature] MG1004  label="MG995_010"
  Placement = pos=(-148.28,-6.40133,4.14478) rot=(-0.574323,0.579357,-0.578358;4.18879rad)
FEATURE [App::LinkGroup] LinkGroup010  label="003002"
  ElementList = -> [MG1004,MG955_horn___Part_010]
  LinkMode = 0
  Placement = pos=(38.2325,-3.15505,14.7276) rot=(0.999997,0.002618,0;3.14159rad)
FEATURE [Sketcher::SketchObject] Sketch050
  FullyConstrained = false
  MapMode = 5
  Support = -> [XY_Plane016]
  sketch-geometry (18):
    g0: ArcOfCircle CenterX=-79.4439 CenterY=0 CenterZ=0 NormalX=0 NormalY=0 NormalZ=1 AngleXU=0 Radius=15 StartAngle=1.5708 EndAngle=4.71239
    g1: ArcOfCircle CenterX=0 CenterY=0 CenterZ=0 NormalX=0 NormalY=0 NormalZ=1 AngleXU=0 Radius=15 StartAngle=4.71239 EndAngle=7.85398
    g2: LineSegment StartX=-79.4439 StartY=-15 StartZ=0 EndX=0 EndY=-15 EndZ=0
    g3: LineSegment StartX=4.6e-15 StartY=15 StartZ=0 EndX=-79.4439 EndY=15 EndZ=0
    g4: Circle CenterX=-83.6435 CenterY=7.0054 CenterZ=0 NormalX=0 NormalY=0 NormalZ=1 AngleXU=0 Radius=1.5
    g5: Circle CenterX=-76.656 CenterY=0 CenterZ=0 NormalX=0 NormalY=0 NormalZ=1 AngleXU=0 Radius=1.5
    g6: Circle CenterX=-90.656 CenterY=0 CenterZ=0 NormalX=0 NormalY=0 NormalZ=1 AngleXU=0 Radius=1.5
    g7: Circle CenterX=-83.6435 CenterY=-6.9946 CenterZ=0 NormalX=0 NormalY=0 NormalZ=1 AngleXU=0 Radius=1.5
    g8: Circle CenterX=-9.95164 CenterY=6.96376 CenterZ=0 NormalX=0 NormalY=0 NormalZ=1 AngleXU=0 Radius=1.5
    g9: Circle CenterX=-2.96346 CenterY=0 CenterZ=0 NormalX=0 NormalY=0 NormalZ=1 AngleXU=0 Radius=1.5
    g10: Circle CenterX=-16.9635 CenterY=0 CenterZ=0 NormalX=0 NormalY=0 NormalZ=1 AngleXU=0 Radius=1.5
    g11: Circle CenterX=-9.95164 CenterY=-7.03624 CenterZ=0 NormalX=0 NormalY=0 NormalZ=1 AngleXU=0 Radius=1.5
    g12: ArcOfCircle CenterX=-60.0538 CenterY=0 CenterZ=0 NormalX=0 NormalY=0 NormalZ=1 AngleXU=0 Radius=7.83101 StartAngle=1.5708 EndAngle=4.71239
    g13: ArcOfCircle CenterX=-32.1156 CenterY=0 CenterZ=0 NormalX=0 NormalY=0 NormalZ=1 AngleXU=0 Radius=7.83101 StartAngle=4.71239 EndAngle=7.85398
    g14: LineSegment StartX=-60.0538 StartY=-7.83101 StartZ=0 EndX=-32.1156 EndY=-7.83101 EndZ=0
    g15: LineSegment StartX=-32.1156 StartY=7.83101 StartZ=0 EndX=-60.0538 EndY=7.83101 EndZ=0
    g16: Circle CenterX=-83.6435 CenterY=0 CenterZ=0 NormalX=0 NormalY=0 NormalZ=1 AngleXU=0 Radius=1.5
    g17: Circle CenterX=-9.95164 CenterY=0 CenterZ=0 NormalX=0 NormalY=0 NormalZ=1 AngleXU=0 Radius=1.5
  constraints (44):
    c: Tangent(g0,g2) = -1.5708
    c: Tangent(g2,g1) = -1.5708
    c: Tangent(g1,g3) = -1.5708
    c: Tangent(g3,g0) = -1.5708
    c: Equal(g0,g1)
    c: PointOnObject(g0,g-1)
    c: Coincident(g1,g-1)
    c: Radius(g1) = 15
    c: PointOnObject(g5,g-1)
    c: PointOnObject(g6,g-1)
    c: Equal(g7,g5)
    c: Equal(g5,g4)
    c: Equal(g4,g6)
    c: Diameter(g4) = 3
    c: Vertical(g4,g7)
    c: DistanceX(g6,g5) = 14
    c: DistanceY(g7,g4) = 14
    c: PointOnObject(g9,g-1)
    c: PointOnObject(g10,g-1)
    c: Equal(g11,g10)
    c: Equal(g10,g8)
    c: Equal(g8,g9)
    c: Diameter(g8) = 3
    c: DistanceX(g10,g9) = 14
    c: DistanceY(g11,g8) = 14
    c: Tangent(g12,g14) = -1.5708
    c: Tangent(g14,g13) = -1.5708
    c: Tangent(g13,g15) = -1.5708
    c: Tangent(g15,g12) = -1.5708
    c: Equal(g12,g13)
    c: PointOnObject(g12,g-1)
    c: PointOnObject(g13,g-1)
    c: PointOnObject(g16,g-1)
    c: PointOnObject(g17,g-1)
    c: Equal(g8,g17)
    c: Equal(g16,g5)
    c: Block(g5)
    c: Block(g4)
    c: Vertical(g16,g7)
    c: Block(g8)
    c: Block(g9)
    c: Vertical(g11,g8)
    c: Vertical(g17,g11)
    c: Block(g15)
FEATURE [PartDesign::Pad] Pad028
  Direction = (0,0,1)
  Length = 3
  Length2 = 10
  Profile = -> Sketch050
  ReferenceAxis = -> Sketch050 [N_Axis]
  Type = 0
FEATURE [Sketcher::SketchObject] Sketch051
  AttachmentOffset = pos=(0,0,1) rot=(0,0,1;0rad)
  FullyConstrained = false
  MapMode = 5
  Placement = pos=(0,0,1) rot=(0,0,1;0rad)
  Support = -> [XY_Plane016]
  sketch-geometry (2):
    g0: Circle CenterX=-10 CenterY=0 CenterZ=0 NormalX=0 NormalY=0 NormalZ=1 AngleXU=0 Radius=10.35
    g1: Circle CenterX=-83.6208 CenterY=0 CenterZ=0 NormalX=0 NormalY=0 NormalZ=1 AngleXU=0 Radius=10.35
  constraints (5):
    c: PointOnObject(g0,g-1)
    c: PointOnObject(g1,g-1)
    c: Equal(g1,g0)
    c: Diameter(g0) = 20.7
    c: DistanceX(g0,g-1) = 10
FEATURE [PartDesign::Pocket] Pocket020
  BaseFeature = -> Pad028
  Direction = (0,0,-1)
  Length = 3
  Length2 = 5
  Profile = -> Sketch051
  ReferenceAxis = -> Sketch051 [N_Axis]
  Reversed = true
  Type = 0
FEATURE [PartDesign::Body] Body016  label="femur_x002"
  Group = -> [Sketch050,Pad028,Sketch051,Pocket020]
  Origin = -> Origin016
  Placement = pos=(0,0,-19) rot=(0,0,1;0rad)
  Tip = -> Pocket020
FEATURE [Sketcher::SketchObject] Sketch052
  FullyConstrained = false
  MapMode = 5
  Support = -> [XY_Plane017]
  sketch-geometry (13):
    g0: LineSegment StartX=-21.5 StartY=-10 StartZ=0 EndX=21.5 EndY=-10 EndZ=0
    g1: LineSegment StartX=21.5 StartY=-10 StartZ=0 EndX=21.5 EndY=10 EndZ=0
    g2: LineSegment StartX=21.5 StartY=10 StartZ=0 EndX=-21.5 EndY=10 EndZ=0
    g3: LineSegment StartX=-21.5 StartY=10 StartZ=0 EndX=-21.5 EndY=-10 EndZ=0
    g4: Circle CenterX=-24.75 CenterY=-5 CenterZ=0 NormalX=0 NormalY=0 NormalZ=1 AngleXU=0 Radius=1.5
    g5: Circle CenterX=-24.75 CenterY=5 CenterZ=0 NormalX=0 NormalY=0 NormalZ=1 AngleXU=0 Radius=1.5
    g6: Circle CenterX=24.75 CenterY=-5 CenterZ=0 NormalX=0 NormalY=0 NormalZ=1 AngleXU=0 Radius=1.5
    g7: Circle CenterX=24.75 CenterY=5 CenterZ=0 NormalX=0 NormalY=0 NormalZ=1 AngleXU=0 Radius=1.5
    g8: LineSegment StartX=27.1868 StartY=-13 StartZ=0 EndX=-21.0434 EndY=-13 EndZ=0
    g9: ArcOfCircle CenterX=-21.0434 CenterY=-2e-16 CenterZ=0 NormalX=0 NormalY=0 NormalZ=1 AngleXU=0 Radius=13 StartAngle=1.5708 EndAngle=4.71239
    g10: LineSegment StartX=-21.0434 StartY=13 StartZ=0 EndX=27.1868 EndY=13 EndZ=0
    g11: LineSegment StartX=27.1868 StartY=13 StartZ=0 EndX=114.981 EndY=1.8e-15 EndZ=0
    g12: LineSegment StartX=27.1868 StartY=-13 StartZ=0 EndX=114.981 EndY=1.8e-15 EndZ=0
  constraints (31):
    c: Coincident(g0,g1)
    c: Coincident(g1,g2)
    c: Coincident(g2,g3)
    c: Coincident(g3,g0)
    c: Horizontal(g0)
    c: Vertical(g1)
    c: Vertical(g3)
    c: DistanceY(g1,g1) = 20
    c: DistanceX(g0,g0) = 43
    c: DistanceY(g0,g-1) = 10
    c: Horizontal(g5,g7)
    c: Horizontal(g4,g6)
    c: Vertical(g6,g7)
    c: Equal(g7,g6)
    c: Equal(g6,g4)
    c: Equal(g4,g5)
    c: Diameter(g6) = 3
    c: Vertical(g5,g4)
    c: DistanceY(g4,g5) = 10
    c: Symmetric(g2,g1,g-2)
    c: Horizontal(g8)
    c: DistanceY(g8,g0) = 3
    c: Coincident(g9,g8)
    c: DistanceY(g2,g9) = 3
    c: Coincident(g10,g9)
    c: Horizontal(g10)
    c: Equal(g10,g8)
    c: Coincident(g11,g10)
    c: PointOnObject(g11,g-1)
    c: Coincident(g12,g8)
    c: Coincident(g12,g11)
FEATURE [PartDesign::Pad] Pad029
  Direction = (0,0,1)
  Length = 3
  Length2 = 10
  Profile = -> Sketch052
  ReferenceAxis = -> Sketch052 [N_Axis]
  Type = 0
FEATURE [PartDesign::Fillet] Fillet013
  Base = -> Pad029 [Edge11]
  BaseFeature = -> Pad029
  Radius = 3
  SupportTransform = false
  UseAllEdges = false
FEATURE [PartDesign::Body] Body017  label="tibia003"
  Group = -> [Sketch052,Pad029,Fillet013]
  Origin = -> Origin017
  Tip = -> Fillet013
FEATURE [Sketcher::SketchObject] Sketch053
  AttachmentOffset = pos=(0,0,-0.25) rot=(0,0,1;0rad)
  FullyConstrained = true
  MapMode = 5
  Placement = pos=(0,0.25,1e-16) rot=(1,0,0;1.5708rad)
  Support = -> [XZ_Plane018]
  sketch-geometry (4):
    g0: LineSegment StartX=-99.4442 StartY=39.7122 StartZ=0 EndX=-97.4442 EndY=39.7122 EndZ=0
    g1: LineSegment StartX=-97.4442 StartY=39.7122 StartZ=0 EndX=-97.4442 EndY=-17.2878 EndZ=0
    g2: LineSegment StartX=-97.4442 StartY=-17.2878 StartZ=0 EndX=-99.4442 EndY=-17.2878 EndZ=0
    g3: LineSegment StartX=-99.4442 StartY=-17.2878 StartZ=0 EndX=-99.4442 EndY=39.7122 EndZ=0
  constraints (11):
    c: Coincident(g0,g1)
    c: Coincident(g1,g2)
    c: Coincident(g2,g3)
    c: Coincident(g3,g0)
    c: Horizontal(g0)
    c: Horizontal(g2)
    c: Vertical(g1)
    c: Vertical(g3)
    c: DistanceX(g2,g2) = 2
    c: DistanceY(g3,g3) = 57
    c: Block(g1)
FEATURE [PartDesign::Pad] Pad030
  Direction = (0,-1,2e-16)
  Length = 30
  Length2 = 10
  Placement = pos=(0,0,0) rot=(1,0,0;1.5708rad)
  Profile = -> Sketch053
  ReferenceAxis = -> Sketch053 [N_Axis]
  Type = 0
FEATURE [Sketcher::SketchObject] Sketch054
  AttachmentOffset = pos=(0,0,-98) rot=(0,0,1;0rad)
  ExternalGeometry = -> [Pad030]
  FullyConstrained = true
  MapMode = 5
  Placement = pos=(-98,2.18e-14,-2.18e-14) rot=(0.57735,0.57735,0.57735;2.0944rad)
  Support = -> [YZ_Plane018]
  sketch-geometry (4):
    g0: LineSegment StartX=-4.75 StartY=39.7122 StartZ=0 EndX=-1.75 EndY=39.7122 EndZ=0
    g1: LineSegment StartX=-1.75 StartY=39.7122 StartZ=0 EndX=-1.75 EndY=-17.2878 EndZ=0
    g2: LineSegment StartX=-1.75 StartY=-17.2878 StartZ=0 EndX=-4.75 EndY=-17.2878 EndZ=0
    g3: LineSegment StartX=-4.75 StartY=-17.2878 StartZ=0 EndX=-4.75 EndY=39.7122 EndZ=0
  constraints (12):
    c: Coincident(g0,g1)
    c: Coincident(g1,g2)
    c: Coincident(g2,g3)
    c: Coincident(g3,g0)
    c: Horizontal(g0)
    c: Horizontal(g2)
    c: Vertical(g1)
    c: Vertical(g3)
    c: PointOnObject(g0,g-3)
    c: PointOnObject(g1,g-4)
    c: DistanceX(g0,g0) = 3
    c: DistanceX(g0,g-3) = 2
FEATURE [PartDesign::Pad] Pad031
  BaseFeature = -> Pad030
  Direction = (1,-2e-16,3e-16)
  Length = 22
  Length2 = 10
  Placement = pos=(0,0,0) rot=(1,0,0;1.5708rad)
  Profile = -> Sketch054
  ReferenceAxis = -> Sketch054 [N_Axis]
  Reversed = true
  Type = 0
FEATURE [Sketcher::SketchObject] Sketch055
  AttachmentOffset = pos=(0,0,-156.5) rot=(0,0,1;0rad)
  FullyConstrained = false
  MapMode = 5
  Placement = pos=(-156.5,3.47e-14,-3.47e-14) rot=(0.57735,0.57735,0.57735;2.0944rad)
  Support = -> [YZ_Plane018]
  sketch-geometry (4):
    g0: LineSegment StartX=-30.4604 StartY=32.0705 StartZ=0 EndX=1.50281 EndY=32.0705 EndZ=0
    g1: LineSegment StartX=1.50281 StartY=32.0705 StartZ=0 EndX=1.50281 EndY=-9.92951 EndZ=0
    g2: LineSegment StartX=1.50281 StartY=-9.92951 StartZ=0 EndX=-30.4604 EndY=-9.92951 EndZ=0
    g3: LineSegment StartX=-30.4604 StartY=-9.92951 StartZ=0 EndX=-30.4604 EndY=32.0705 EndZ=0
  constraints (9):
    c: Coincident(g0,g1)
    c: Coincident(g1,g2)
    c: Coincident(g2,g3)
    c: Coincident(g3,g0)
    c: Horizontal(g0)
    c: Horizontal(g2)
    c: Vertical(g1)
    c: Vertical(g3)
    c: DistanceY(g1,g1) = 42
FEATURE [PartDesign::Pocket] Pocket021
  BaseFeature = -> Pad031
  Direction = (-1,2e-16,-3e-16)
  Length = 0
  Length2 = 5
  Placement = pos=(0,0,0) rot=(1,0,0;1.5708rad)
  Profile = -> Sketch055
  ReferenceAxis = -> Sketch055 [N_Axis]
  Type = 3
  UpToFace = -> Pad031 [Face5]
FEATURE [Sketcher::SketchObject] Sketch056
  FullyConstrained = true
  MapMode = 5
  Placement = pos=(0,0,0) rot=(1,0,0;1.5708rad)
  Support = -> [XZ_Plane018]
  sketch-geometry (4):
    g0: Circle CenterX=-114.988 CenterY=36.3647 CenterZ=0 NormalX=0 NormalY=0 NormalZ=1 AngleXU=0 Radius=1.5
    g1: Circle CenterX=-105.112 CenterY=36.3647 CenterZ=0 NormalX=0 NormalY=0 NormalZ=1 AngleXU=0 Radius=1.5
    g2: Circle CenterX=-114.988 CenterY=-13.0424 CenterZ=0 NormalX=0 NormalY=0 NormalZ=1 AngleXU=0 Radius=1.5
    g3: Circle CenterX=-104.988 CenterY=-13.0424 CenterZ=0 NormalX=0 NormalY=0 NormalZ=1 AngleXU=0 Radius=1.5
  constraints (11):
    c: Horizontal(g3,g2)
    c: Horizontal(g0,g1)
    c: Vertical(g0,g2)
    c: Diameter(g1) = 3
    c: Equal(g0,g1)
    c: Equal(g2,g3)
    c: Equal(g3,g1)
    c: DistanceX(g2,g3) = 10
    c: Block(g1)
    c: Block(g0)
    c: Block(g2)
FEATURE [PartDesign::Pocket] Pocket022
  BaseFeature = -> Pocket021
  Direction = (0,1,-2e-16)
  Length = 5
  Length2 = 5
  Placement = pos=(0,0,0) rot=(1,0,0;1.5708rad)
  Profile = -> Sketch056
  ReferenceAxis = -> Sketch056 [N_Axis]
  Reversed = true
  Type = 1
FEATURE [Sketcher::SketchObject] Sketch057
  AttachmentOffset = pos=(0,0,-18) rot=(0,0,1;0rad)
  FullyConstrained = true
  MapMode = 5
  Placement = pos=(0,18,4e-15) rot=(1,0,0;1.5708rad)
  Support = -> [XZ_Plane019]
  sketch-geometry (4):
    g0: LineSegment StartX=-97.0237 StartY=39.7039 StartZ=0 EndX=-95.0237 EndY=39.7039 EndZ=0
    g1: LineSegment StartX=-95.0237 StartY=39.7039 StartZ=0 EndX=-95.0237 EndY=-17.2961 EndZ=0
    g2: LineSegment StartX=-95.0237 StartY=-17.2961 StartZ=0 EndX=-97.0237 EndY=-17.2961 EndZ=0
    g3: LineSegment StartX=-97.0237 StartY=-17.2961 StartZ=0 EndX=-97.0237 EndY=39.7039 EndZ=0
  constraints (11):
    c: Coincident(g0,g1)
    c: Coincident(g1,g2)
    c: Coincident(g3,g0)
    c: Horizontal(g0)
    c: Horizontal(g2)
    c: Vertical(g1)
    c: Vertical(g3)
    c: DistanceX(g0,g0) = 2
    c: Coincident(g3,g2)
    c: DistanceY(g1,g1) = 57
    c: Block(g1)
FEATURE [PartDesign::Pad] Pad032
  Direction = (0,-1,2e-16)
  Length = 56
  Length2 = 10
  Placement = pos=(0,0,0) rot=(1,0,0;1.5708rad)
  Profile = -> Sketch057
  ReferenceAxis = -> Sketch057 [N_Axis]
  Type = 0
FEATURE [Sketcher::SketchObject] Sketch058
  AttachmentOffset = pos=(0,0,-74) rot=(0,0,1;0rad)
  ExternalGeometry = -> [Pad032]
  FullyConstrained = true
  MapMode = 5
  Placement = pos=(-74,1.64e-14,-1.64e-14) rot=(0.57735,0.57735,0.57735;2.0944rad)
  Support = -> [YZ_Plane019]
  sketch-geometry (4):
    g0: LineSegment StartX=-38 StartY=0 StartZ=0 EndX=18 EndY=0 EndZ=0
    g1: LineSegment StartX=18 StartY=0 StartZ=0 EndX=18 EndY=4 EndZ=0
    g2: LineSegment StartX=18 StartY=4 StartZ=0 EndX=-38 EndY=4 EndZ=0
    g3: LineSegment StartX=-38 StartY=4 StartZ=0 EndX=-38 EndY=0 EndZ=0
  constraints (12):
    c: Coincident(g0,g1)
    c: Coincident(g1,g2)
    c: Coincident(g2,g3)
    c: Coincident(g3,g0)
    c: Horizontal(g0)
    c: Horizontal(g2)
    c: Vertical(g1)
    c: Vertical(g3)
    c: PointOnObject(g0,g-3)
    c: PointOnObject(g1,g-4)
    c: PointOnObject(g0,g-1)
    c: DistanceY(g1,g1) = 4
FEATURE [PartDesign::Pad] Pad033
  BaseFeature = -> Pad032
  Direction = (1,-2e-16,3e-16)
  Length = 10
  Length2 = 10
  Placement = pos=(0,0,0) rot=(1,0,0;1.5708rad)
  Profile = -> Sketch058
  ReferenceAxis = -> Sketch058 [N_Axis]
  Type = 3
  UpToFace = -> Pad032 [Face2]
FEATURE [Sketcher::SketchObject] Sketch059
  FullyConstrained = false
  MapMode = 5
  Placement = pos=(0,0,0) rot=(0.57735,0.57735,0.57735;2.0944rad)
  Support = -> [YZ_Plane019]
  sketch-geometry (4):
    g0: LineSegment StartX=-30.4465 StartY=4.63736 StartZ=0 EndX=10.5535 EndY=4.63736 EndZ=0
    g1: LineSegment StartX=10.5535 StartY=4.63736 StartZ=0 EndX=10.5535 EndY=-3.9404 EndZ=0
    g2: LineSegment StartX=10.5535 StartY=-3.9404 StartZ=0 EndX=-30.4465 EndY=-3.9404 EndZ=0
    g3: LineSegment StartX=-30.4465 StartY=-3.9404 StartZ=0 EndX=-30.4465 EndY=4.63736 EndZ=0
  constraints (9):
    c: Coincident(g0,g1)
    c: Coincident(g1,g2)
    c: Coincident(g2,g3)
    c: Coincident(g3,g0)
    c: Horizontal(g0)
    c: Horizontal(g2)
    c: Vertical(g1)
    c: Vertical(g3)
    c: DistanceX(g0,g0) = 41
FEATURE [PartDesign::Pocket] Pocket023
  BaseFeature = -> Pad033
  Direction = (-1,2e-16,-3e-16)
  Length = 0
  Length2 = 5
  Placement = pos=(0,0,0) rot=(1,0,0;1.5708rad)
  Profile = -> Sketch059
  ReferenceAxis = -> Sketch059 [N_Axis]
  Type = 3
  UpToFace = -> Pad033 [Face9]
FEATURE [Sketcher::SketchObject] Sketch060
  FullyConstrained = true
  MapMode = 5
  Support = -> [XY_Plane019]
  sketch-geometry (4):
    g0: Circle CenterX=-88.7181 CenterY=14.6635 CenterZ=0 NormalX=0 NormalY=0 NormalZ=1 AngleXU=0 Radius=1.5
    g1: Circle CenterX=-78.7181 CenterY=14.6635 CenterZ=0 NormalX=0 NormalY=0 NormalZ=1 AngleXU=0 Radius=1.5
    g2: Circle CenterX=-88.7181 CenterY=-34.6965 CenterZ=0 NormalX=0 NormalY=0 NormalZ=1 AngleXU=0 Radius=1.5
    g3: Circle CenterX=-78.7181 CenterY=-34.6965 CenterZ=0 NormalX=0 NormalY=0 NormalZ=1 AngleXU=0 Radius=1.5
  constraints (11):
    c: Equal(g3,g2)
    c: Equal(g3,g1)
    c: Equal(g3,g0)
    c: Diameter(g3) = 3
    c: Horizontal(g0,g1)
    c: DistanceX(g0,g1) = 10
    c: Horizontal(g2,g3)
    c: DistanceX(g2,g3) = 10
    c: Vertical(g2,g0)
    c: Block(g1)
    c: Block(g2)
FEATURE [PartDesign::Pocket] Pocket024
  BaseFeature = -> Pocket023
  Direction = (0,0,-1)
  Length = 5
  Length2 = 5
  Placement = pos=(0,0,0) rot=(1,0,0;1.5708rad)
  Profile = -> Sketch060
  ReferenceAxis = -> Sketch060 [N_Axis]
  Reversed = true
  Type = 1
FEATURE [Sketcher::SketchObject] Sketch061
  AttachmentOffset = pos=(0,0,-1) rot=(0,0,1;0rad)
  FullyConstrained = false
  MapMode = 5
  Placement = pos=(0,1,2e-16) rot=(1,0,0;1.5708rad)
  Support = -> [XZ_Plane018]
  sketch-geometry (4):
    g0: LineSegment StartX=-101.574 StartY=41.4203 StartZ=0 EndX=-97.0564 EndY=41.4203 EndZ=0
    g1: LineSegment StartX=-97.0564 StartY=41.4203 StartZ=0 EndX=-97.0564 EndY=-19.084 EndZ=0
    g2: LineSegment StartX=-97.0564 StartY=-19.084 StartZ=0 EndX=-101.574 EndY=-19.084 EndZ=0
    g3: LineSegment StartX=-101.574 StartY=-19.084 StartZ=0 EndX=-101.574 EndY=41.4203 EndZ=0
  constraints (8):
    c: Coincident(g0,g1)
    c: Coincident(g1,g2)
    c: Coincident(g2,g3)
    c: Coincident(g3,g0)
    c: Horizontal(g0)
    c: Horizontal(g2)
    c: Vertical(g1)
    c: Vertical(g3)
FEATURE [PartDesign::Pocket] Pocket025
  BaseFeature = -> Pocket022
  Direction = (0,1,-2e-16)
  Length = 0
  Length2 = 5
  Placement = pos=(0,0,0) rot=(1,0,0;1.5708rad)
  Profile = -> Sketch061
  ReferenceAxis = -> Sketch061 [N_Axis]
  Reversed = true
  Type = 3
  UpToFace = -> Pocket022 [Face17]
FEATURE [PartDesign::Fillet] Fillet014
  Base = -> Pocket025 [Edge57,Edge63,Edge36,Edge51]
  BaseFeature = -> Pocket025
  Placement = pos=(0,0,0) rot=(1,0,0;1.5708rad)
  Radius = 3
  SupportTransform = false
  UseAllEdges = false
FEATURE [Sketcher::SketchObject] Sketch062
  FullyConstrained = false
  MapMode = 5
  Placement = pos=(0,0,0) rot=(0.57735,0.57735,0.57735;2.0944rad)
  Support = -> [YZ_Plane019]
  sketch-geometry (4):
    g0: Circle CenterX=-11.1549 CenterY=35.9602 CenterZ=0 NormalX=0 NormalY=0 NormalZ=1 AngleXU=0 Radius=1.5
    g1: Circle CenterX=-21.1549 CenterY=35.9602 CenterZ=0 NormalX=0 NormalY=0 NormalZ=1 AngleXU=0 Radius=1.5
    g2: Circle CenterX=-11.1549 CenterY=-13.701 CenterZ=0 NormalX=0 NormalY=0 NormalZ=1 AngleXU=0 Radius=1.5
    g3: Circle CenterX=-21.1549 CenterY=-13.701 CenterZ=0 NormalX=0 NormalY=0 NormalZ=1 AngleXU=0 Radius=1.5
  constraints (9):
    c: Equal(g0,g1)
    c: Diameter(g0) = 3
    c: DistanceX(g1,g0) = 10
    c: Horizontal(g0,g1)
    c: Equal(g3,g2)
    c: Diameter(g3) = 3
    c: Horizontal(g2,g3)
    c: DistanceX(g3,g2) = 10
    c: Vertical(g2,g0)
FEATURE [PartDesign::Pocket] Pocket026
  BaseFeature = -> Pocket024
  Direction = (-1,2e-16,-3e-16)
  Length = 0
  Length2 = 5
  Placement = pos=(0,0,0) rot=(1,0,0;1.5708rad)
  Profile = -> Sketch062
  ReferenceAxis = -> Sketch062 [N_Axis]
  Reversed = true
  Type = 3
  UpToFace = -> Fillet014 [Face4]
FEATURE [PartDesign::Fillet] Fillet015
  Base = -> Pocket026 [Edge64,Edge52,Edge54,Edge45]
  BaseFeature = -> Pocket026
  Placement = pos=(0,0,0) rot=(1,0,0;1.5708rad)
  Radius = 3
  SupportTransform = false
  UseAllEdges = false
FEATURE [PartDesign::Fillet] Fillet016
  Base = -> Fillet015 [Edge36,Edge34,Edge45,Edge42]
  BaseFeature = -> Fillet015
  Placement = pos=(0,0,0) rot=(1,0,0;1.5708rad)
  Radius = 10
  SupportTransform = false
  UseAllEdges = false
FEATURE [PartDesign::Body] Body019  label="coxa_006"
  Group = -> [Sketch057,Pad032,Sketch058,Pad033,Sketch059,Pocket023,Sketch060,Pocket024,Sketch062,Pocket026,Fillet015,Fillet016]
  Origin = -> Origin019
  Placement = pos=(0,20.26,0) rot=(0,0,1;0rad)
  Tip = -> Fillet016
FEATURE [Sketcher::SketchObject] Sketch063
  FullyConstrained = true
  MapMode = 5
  Placement = pos=(0,0,0) rot=(0.57735,0.57735,0.57735;2.0944rad)
  Support = -> [YZ_Plane018]
  sketch-geometry (4):
    g0: Circle CenterX=-21.1481 CenterY=35.969 CenterZ=0 NormalX=0 NormalY=0 NormalZ=1 AngleXU=0 Radius=1.5
    g1: Circle CenterX=-11.1481 CenterY=35.969 CenterZ=0 NormalX=0 NormalY=0 NormalZ=1 AngleXU=0 Radius=1.5
    g2: Circle CenterX=-21.1481 CenterY=-13.7095 CenterZ=0 NormalX=0 NormalY=0 NormalZ=1 AngleXU=0 Radius=1.5
    g3: Circle CenterX=-11.1481 CenterY=-13.7095 CenterZ=0 NormalX=0 NormalY=0 NormalZ=1 AngleXU=0 Radius=1.5
  constraints (11):
    c: Equal(g3,g2)
    c: Equal(g3,g0)
    c: Equal(g3,g1)
    c: Diameter(g3) = 3
    c: Horizontal(g0,g1)
    c: DistanceX(g0,g1) = 10
    c: Horizontal(g2,g3)
    c: DistanceX(g2,g3) = 10
    c: Vertical(g2,g0)
    c: Block(g1)
    c: Block(g2)
FEATURE [PartDesign::Pocket] Pocket027
  BaseFeature = -> Fillet014
  Direction = (-1,2e-16,-3e-16)
  Length = 0
  Length2 = 5
  Placement = pos=(0,0,0) rot=(1,0,0;1.5708rad)
  Profile = -> Sketch063
  ReferenceAxis = -> Sketch063 [N_Axis]
  Type = 3
  UpToFace = -> Fillet014 [Face4]
FEATURE [PartDesign::Body] Body018  label="coxa_005"
  Group = -> [Sketch053,Pad030,Sketch054,Pad031,Sketch055,Pocket021,Sketch056,Pocket022,Sketch061,Pocket025,Fillet014,Sketch063,Pocket027]
  Origin = -> Origin018
  Placement = pos=(0,0.645604,21.6579) rot=(1,0,0;3.1381rad)
  Tip = -> Pocket027
FEATURE [App::LinkGroup] LinkGroup013  label="LegFR"
  ElementList = -> [Body016,LinkGroup012,LinkGroup011,LinkGroup010,Body018,Body019,Body017]
  LinkMode = 0
  Placement = pos=(-294.25,0.987527,51.44) rot=(0,0,1;3.1381rad)
FEATURE [Mesh::Feature] MG1005  label="MG995_011"
FEATURE [Mesh::Feature] MG1006  label="MG995_012"
  Placement = pos=(-83.7023,-10.014,0) rot=(0,0,-1;1.57429rad)
FEATURE [Mesh::Feature] MG1007  label="MG995_013"
  Placement = pos=(-148.28,-6.40133,4.14478) rot=(-0.574323,0.579357,-0.578358;4.18879rad)
FEATURE [Mesh::Feature] MG955_horn___Part_012  label="MG955 horn - 011"
  Placement = pos=(-9.96,-0.03,-15.72) rot=(1,0,0;4.71239rad)
FEATURE [App::LinkGroup] LinkGroup015  label="001002001"
  ElementList = -> [MG955_horn___Part_012,MG1005]
  LinkMode = 0
FEATURE [Mesh::Feature] MG955_horn___Part_013  label="MG955 horn - 012"
  Placement = pos=(-148.18,9.46278,-5.87693) rot=(-1,0,0;6.28144rad)
FEATURE [App::LinkGroup] LinkGroup014  label="003002001"
  ElementList = -> [MG1007,MG955_horn___Part_013]
  LinkMode = 0
  Placement = pos=(-258.556,-2.79406,6.61252) rot=(-0.002618,-2.4e-05,0.999997;3.13391rad)
FEATURE [Mesh::Feature] MG955_horn___Part_014  label="MG955 horn - 013"
  Placement = pos=(-83.66,-0.03,-15.72) rot=(1,0,0;4.71239rad)
FEATURE [App::LinkGroup] LinkGroup016  label="002002001"
  ElementList = -> [MG955_horn___Part_014,MG1006]
  LinkMode = 0
  Placement = pos=(-167.334,-0.319952,-4.76837e-07) rot=(0,0,1;3.14508rad)
FEATURE [Sketcher::SketchObject] Sketch064
  FullyConstrained = false
  MapMode = 5
  Support = -> [XY_Plane020]
  sketch-geometry (18):
    g0: ArcOfCircle CenterX=-79.4439 CenterY=0 CenterZ=0 NormalX=0 NormalY=0 NormalZ=1 AngleXU=0 Radius=15 StartAngle=1.5708 EndAngle=4.71239
    g1: ArcOfCircle CenterX=0 CenterY=0 CenterZ=0 NormalX=0 NormalY=0 NormalZ=1 AngleXU=0 Radius=15 StartAngle=4.71239 EndAngle=7.85398
    g2: LineSegment StartX=-79.4439 StartY=-15 StartZ=0 EndX=0 EndY=-15 EndZ=0
    g3: LineSegment StartX=4.6e-15 StartY=15 StartZ=0 EndX=-79.4439 EndY=15 EndZ=0
    g4: Circle CenterX=-83.6435 CenterY=7.0054 CenterZ=0 NormalX=0 NormalY=0 NormalZ=1 AngleXU=0 Radius=1.5
    g5: Circle CenterX=-76.656 CenterY=0 CenterZ=0 NormalX=0 NormalY=0 NormalZ=1 AngleXU=0 Radius=1.5
    g6: Circle CenterX=-90.656 CenterY=0 CenterZ=0 NormalX=0 NormalY=0 NormalZ=1 AngleXU=0 Radius=1.5
    g7: Circle CenterX=-83.6435 CenterY=-6.9946 CenterZ=0 NormalX=0 NormalY=0 NormalZ=1 AngleXU=0 Radius=1.5
    g8: Circle CenterX=-9.95164 CenterY=6.96376 CenterZ=0 NormalX=0 NormalY=0 NormalZ=1 AngleXU=0 Radius=1.5
    g9: Circle CenterX=-2.96346 CenterY=0 CenterZ=0 NormalX=0 NormalY=0 NormalZ=1 AngleXU=0 Radius=1.5
    g10: Circle CenterX=-16.9635 CenterY=0 CenterZ=0 NormalX=0 NormalY=0 NormalZ=1 AngleXU=0 Radius=1.5
    g11: Circle CenterX=-9.95164 CenterY=-7.03624 CenterZ=0 NormalX=0 NormalY=0 NormalZ=1 AngleXU=0 Radius=1.5
    g12: ArcOfCircle CenterX=-60.0538 CenterY=0 CenterZ=0 NormalX=0 NormalY=0 NormalZ=1 AngleXU=0 Radius=7.83101 StartAngle=1.5708 EndAngle=4.71239
    g13: ArcOfCircle CenterX=-32.1156 CenterY=0 CenterZ=0 NormalX=0 NormalY=0 NormalZ=1 AngleXU=0 Radius=7.83101 StartAngle=4.71239 EndAngle=7.85398
    g14: LineSegment StartX=-60.0538 StartY=-7.83101 StartZ=0 EndX=-32.1156 EndY=-7.83101 EndZ=0
    g15: LineSegment StartX=-32.1156 StartY=7.83101 StartZ=0 EndX=-60.0538 EndY=7.83101 EndZ=0
    g16: Circle CenterX=-83.6435 CenterY=0 CenterZ=0 NormalX=0 NormalY=0 NormalZ=1 AngleXU=0 Radius=1.5
    g17: Circle CenterX=-9.95164 CenterY=0 CenterZ=0 NormalX=0 NormalY=0 NormalZ=1 AngleXU=0 Radius=1.5
  constraints (44):
    c: Tangent(g0,g2) = -1.5708
    c: Tangent(g2,g1) = -1.5708
    c: Tangent(g1,g3) = -1.5708
    c: Tangent(g3,g0) = -1.5708
    c: Equal(g0,g1)
    c: PointOnObject(g0,g-1)
    c: Coincident(g1,g-1)
    c: Radius(g1) = 15
    c: PointOnObject(g5,g-1)
    c: PointOnObject(g6,g-1)
    c: Equal(g7,g5)
    c: Equal(g5,g4)
    c: Equal(g4,g6)
    c: Diameter(g4) = 3
    c: Vertical(g4,g7)
    c: DistanceX(g6,g5) = 14
    c: DistanceY(g7,g4) = 14
    c: PointOnObject(g9,g-1)
    c: PointOnObject(g10,g-1)
    c: Equal(g11,g10)
    c: Equal(g10,g8)
    c: Equal(g8,g9)
    c: Diameter(g8) = 3
    c: DistanceX(g10,g9) = 14
    c: DistanceY(g11,g8) = 14
    c: Tangent(g12,g14) = -1.5708
    c: Tangent(g14,g13) = -1.5708
    c: Tangent(g13,g15) = -1.5708
    c: Tangent(g15,g12) = -1.5708
    c: Equal(g12,g13)
    c: PointOnObject(g12,g-1)
    c: PointOnObject(g13,g-1)
    c: PointOnObject(g16,g-1)
    c: PointOnObject(g17,g-1)
    c: Equal(g8,g17)
    c: Equal(g16,g5)
    c: Block(g5)
    c: Block(g4)
    c: Vertical(g16,g7)
    c: Block(g8)
    c: Block(g9)
    c: Vertical(g11,g8)
    c: Vertical(g17,g11)
    c: Block(g15)
FEATURE [PartDesign::Pad] Pad034
  Direction = (0,0,1)
  Length = 3
  Length2 = 10
  Profile = -> Sketch064
  ReferenceAxis = -> Sketch064 [N_Axis]
  Type = 0
FEATURE [Sketcher::SketchObject] Sketch065
  AttachmentOffset = pos=(0,0,1) rot=(0,0,1;0rad)
  FullyConstrained = false
  MapMode = 5
  Placement = pos=(0,0,1) rot=(0,0,1;0rad)
  Support = -> [XY_Plane020]
  sketch-geometry (2):
    g0: Circle CenterX=-10 CenterY=0 CenterZ=0 NormalX=0 NormalY=0 NormalZ=1 AngleXU=0 Radius=10.35
    g1: Circle CenterX=-83.6208 CenterY=0 CenterZ=0 NormalX=0 NormalY=0 NormalZ=1 AngleXU=0 Radius=10.35
  constraints (5):
    c: PointOnObject(g0,g-1)
    c: PointOnObject(g1,g-1)
    c: Equal(g1,g0)
    c: Diameter(g0) = 20.7
    c: DistanceX(g0,g-1) = 10
FEATURE [PartDesign::Pocket] Pocket028
  BaseFeature = -> Pad034
  Direction = (0,0,-1)
  Length = 3
  Length2 = 5
  Profile = -> Sketch065
  ReferenceAxis = -> Sketch065 [N_Axis]
  Reversed = true
  Type = 0
FEATURE [PartDesign::Body] Body020  label="femur_x003"
  Group = -> [Sketch064,Pad034,Sketch065,Pocket028]
  Origin = -> Origin020
  Placement = pos=(0,0,-19) rot=(0,0,1;0rad)
  Tip = -> Pocket028
FEATURE [Sketcher::SketchObject] Sketch066
  FullyConstrained = false
  MapMode = 5
  Support = -> [XY_Plane021]
  sketch-geometry (13):
    g0: LineSegment StartX=-21.5 StartY=-10 StartZ=0 EndX=21.5 EndY=-10 EndZ=0
    g1: LineSegment StartX=21.5 StartY=-10 StartZ=0 EndX=21.5 EndY=10 EndZ=0
    g2: LineSegment StartX=21.5 StartY=10 StartZ=0 EndX=-21.5 EndY=10 EndZ=0
    g3: LineSegment StartX=-21.5 StartY=10 StartZ=0 EndX=-21.5 EndY=-10 EndZ=0
    g4: Circle CenterX=-24.75 CenterY=-5 CenterZ=0 NormalX=0 NormalY=0 NormalZ=1 AngleXU=0 Radius=1.5
    g5: Circle CenterX=-24.75 CenterY=5 CenterZ=0 NormalX=0 NormalY=0 NormalZ=1 AngleXU=0 Radius=1.5
    g6: Circle CenterX=24.75 CenterY=-5 CenterZ=0 NormalX=0 NormalY=0 NormalZ=1 AngleXU=0 Radius=1.5
    g7: Circle CenterX=24.75 CenterY=5 CenterZ=0 NormalX=0 NormalY=0 NormalZ=1 AngleXU=0 Radius=1.5
    g8: LineSegment StartX=27.1868 StartY=-13 StartZ=0 EndX=-21.0434 EndY=-13 EndZ=0
    g9: ArcOfCircle CenterX=-21.0434 CenterY=-2e-16 CenterZ=0 NormalX=0 NormalY=0 NormalZ=1 AngleXU=0 Radius=13 StartAngle=1.5708 EndAngle=4.71239
    g10: LineSegment StartX=-21.0434 StartY=13 StartZ=0 EndX=27.1868 EndY=13 EndZ=0
    g11: LineSegment StartX=27.1868 StartY=13 StartZ=0 EndX=114.981 EndY=1.8e-15 EndZ=0
    g12: LineSegment StartX=27.1868 StartY=-13 StartZ=0 EndX=114.981 EndY=1.8e-15 EndZ=0
  constraints (31):
    c: Coincident(g0,g1)
    c: Coincident(g1,g2)
    c: Coincident(g2,g3)
    c: Coincident(g3,g0)
    c: Horizontal(g0)
    c: Vertical(g1)
    c: Vertical(g3)
    c: DistanceY(g1,g1) = 20
    c: DistanceX(g0,g0) = 43
    c: DistanceY(g0,g-1) = 10
    c: Horizontal(g5,g7)
    c: Horizontal(g4,g6)
    c: Vertical(g6,g7)
    c: Equal(g7,g6)
    c: Equal(g6,g4)
    c: Equal(g4,g5)
    c: Diameter(g6) = 3
    c: Vertical(g5,g4)
    c: DistanceY(g4,g5) = 10
    c: Symmetric(g2,g1,g-2)
    c: Horizontal(g8)
    c: DistanceY(g8,g0) = 3
    c: Coincident(g9,g8)
    c: DistanceY(g2,g9) = 3
    c: Coincident(g10,g9)
    c: Horizontal(g10)
    c: Equal(g10,g8)
    c: Coincident(g11,g10)
    c: PointOnObject(g11,g-1)
    c: Coincident(g12,g8)
    c: Coincident(g12,g11)
FEATURE [PartDesign::Pad] Pad035
  Direction = (0,0,1)
  Length = 3
  Length2 = 10
  Profile = -> Sketch066
  ReferenceAxis = -> Sketch066 [N_Axis]
  Type = 0
FEATURE [PartDesign::Fillet] Fillet017
  Base = -> Pad035 [Edge11]
  BaseFeature = -> Pad035
  Radius = 3
  SupportTransform = false
  UseAllEdges = false
FEATURE [PartDesign::Body] Body021  label="tibia004"
  Group = -> [Sketch066,Pad035,Fillet017]
  Origin = -> Origin021
  Tip = -> Fillet017
FEATURE [Sketcher::SketchObject] Sketch067
  AttachmentOffset = pos=(0,0,-0.25) rot=(0,0,1;0rad)
  FullyConstrained = true
  MapMode = 5
  Placement = pos=(0,0.25,1e-16) rot=(1,0,0;1.5708rad)
  Support = -> [XZ_Plane022]
  sketch-geometry (4):
    g0: LineSegment StartX=-99.4442 StartY=39.7122 StartZ=0 EndX=-97.4442 EndY=39.7122 EndZ=0
    g1: LineSegment StartX=-97.4442 StartY=39.7122 StartZ=0 EndX=-97.4442 EndY=-17.2878 EndZ=0
    g2: LineSegment StartX=-97.4442 StartY=-17.2878 StartZ=0 EndX=-99.4442 EndY=-17.2878 EndZ=0
    g3: LineSegment StartX=-99.4442 StartY=-17.2878 StartZ=0 EndX=-99.4442 EndY=39.7122 EndZ=0
  constraints (11):
    c: Coincident(g0,g1)
    c: Coincident(g1,g2)
    c: Coincident(g2,g3)
    c: Coincident(g3,g0)
    c: Horizontal(g0)
    c: Horizontal(g2)
    c: Vertical(g1)
    c: Vertical(g3)
    c: DistanceX(g2,g2) = 2
    c: DistanceY(g3,g3) = 57
    c: Block(g1)
FEATURE [PartDesign::Pad] Pad036
  Direction = (0,-1,2e-16)
  Length = 30
  Length2 = 10
  Placement = pos=(0,0,0) rot=(1,0,0;1.5708rad)
  Profile = -> Sketch067
  ReferenceAxis = -> Sketch067 [N_Axis]
  Type = 0
FEATURE [Sketcher::SketchObject] Sketch068
  AttachmentOffset = pos=(0,0,-98) rot=(0,0,1;0rad)
  ExternalGeometry = -> [Pad036]
  FullyConstrained = true
  MapMode = 5
  Placement = pos=(-98,2.18e-14,-2.18e-14) rot=(0.57735,0.57735,0.57735;2.0944rad)
  Support = -> [YZ_Plane022]
  sketch-geometry (4):
    g0: LineSegment StartX=-4.75 StartY=39.7122 StartZ=0 EndX=-1.75 EndY=39.7122 EndZ=0
    g1: LineSegment StartX=-1.75 StartY=39.7122 StartZ=0 EndX=-1.75 EndY=-17.2878 EndZ=0
    g2: LineSegment StartX=-1.75 StartY=-17.2878 StartZ=0 EndX=-4.75 EndY=-17.2878 EndZ=0
    g3: LineSegment StartX=-4.75 StartY=-17.2878 StartZ=0 EndX=-4.75 EndY=39.7122 EndZ=0
  constraints (12):
    c: Coincident(g0,g1)
    c: Coincident(g1,g2)
    c: Coincident(g2,g3)
    c: Coincident(g3,g0)
    c: Horizontal(g0)
    c: Horizontal(g2)
    c: Vertical(g1)
    c: Vertical(g3)
    c: PointOnObject(g0,g-3)
    c: PointOnObject(g1,g-4)
    c: DistanceX(g0,g0) = 3
    c: DistanceX(g0,g-3) = 2
FEATURE [PartDesign::Pad] Pad037
  BaseFeature = -> Pad036
  Direction = (1,-2e-16,3e-16)
  Length = 22
  Length2 = 10
  Placement = pos=(0,0,0) rot=(1,0,0;1.5708rad)
  Profile = -> Sketch068
  ReferenceAxis = -> Sketch068 [N_Axis]
  Reversed = true
  Type = 0
FEATURE [Sketcher::SketchObject] Sketch069
  AttachmentOffset = pos=(0,0,-156.5) rot=(0,0,1;0rad)
  FullyConstrained = false
  MapMode = 5
  Placement = pos=(-156.5,3.47e-14,-3.47e-14) rot=(0.57735,0.57735,0.57735;2.0944rad)
  Support = -> [YZ_Plane022]
  sketch-geometry (4):
    g0: LineSegment StartX=-30.4604 StartY=32.0705 StartZ=0 EndX=1.50281 EndY=32.0705 EndZ=0
    g1: LineSegment StartX=1.50281 StartY=32.0705 StartZ=0 EndX=1.50281 EndY=-9.92951 EndZ=0
    g2: LineSegment StartX=1.50281 StartY=-9.92951 StartZ=0 EndX=-30.4604 EndY=-9.92951 EndZ=0
    g3: LineSegment StartX=-30.4604 StartY=-9.92951 StartZ=0 EndX=-30.4604 EndY=32.0705 EndZ=0
  constraints (9):
    c: Coincident(g0,g1)
    c: Coincident(g1,g2)
    c: Coincident(g2,g3)
    c: Coincident(g3,g0)
    c: Horizontal(g0)
    c: Horizontal(g2)
    c: Vertical(g1)
    c: Vertical(g3)
    c: DistanceY(g1,g1) = 42
FEATURE [PartDesign::Pocket] Pocket029
  BaseFeature = -> Pad037
  Direction = (-1,2e-16,-3e-16)
  Length = 0
  Length2 = 5
  Placement = pos=(0,0,0) rot=(1,0,0;1.5708rad)
  Profile = -> Sketch069
  ReferenceAxis = -> Sketch069 [N_Axis]
  Type = 3
  UpToFace = -> Pad037 [Face5]
FEATURE [Sketcher::SketchObject] Sketch070
  FullyConstrained = true
  MapMode = 5
  Placement = pos=(0,0,0) rot=(1,0,0;1.5708rad)
  Support = -> [XZ_Plane022]
  sketch-geometry (4):
    g0: Circle CenterX=-114.988 CenterY=36.3647 CenterZ=0 NormalX=0 NormalY=0 NormalZ=1 AngleXU=0 Radius=1.5
    g1: Circle CenterX=-105.112 CenterY=36.3647 CenterZ=0 NormalX=0 NormalY=0 NormalZ=1 AngleXU=0 Radius=1.5
    g2: Circle CenterX=-114.988 CenterY=-13.0424 CenterZ=0 NormalX=0 NormalY=0 NormalZ=1 AngleXU=0 Radius=1.5
    g3: Circle CenterX=-104.988 CenterY=-13.0424 CenterZ=0 NormalX=0 NormalY=0 NormalZ=1 AngleXU=0 Radius=1.5
  constraints (11):
    c: Horizontal(g3,g2)
    c: Horizontal(g0,g1)
    c: Vertical(g0,g2)
    c: Diameter(g1) = 3
    c: Equal(g0,g1)
    c: Equal(g2,g3)
    c: Equal(g3,g1)
    c: DistanceX(g2,g3) = 10
    c: Block(g1)
    c: Block(g0)
    c: Block(g2)
FEATURE [PartDesign::Pocket] Pocket030
  BaseFeature = -> Pocket029
  Direction = (0,1,2e-16)
  Length = 5
  Length2 = 5
  Placement = pos=(0,0,0) rot=(1,0,0;1.5708rad)
  Profile = -> Sketch070
  ReferenceAxis = -> Sketch070 [N_Axis]
  Reversed = true
  Type = 1
FEATURE [Sketcher::SketchObject] Sketch071
  AttachmentOffset = pos=(0,0,-18) rot=(0,0,1;0rad)
  FullyConstrained = true
  MapMode = 5
  Placement = pos=(0,18,4e-15) rot=(1,0,0;1.5708rad)
  Support = -> [XZ_Plane023]
  sketch-geometry (4):
    g0: LineSegment StartX=-97.0237 StartY=39.7039 StartZ=0 EndX=-95.0237 EndY=39.7039 EndZ=0
    g1: LineSegment StartX=-95.0237 StartY=39.7039 StartZ=0 EndX=-95.0237 EndY=-17.2961 EndZ=0
    g2: LineSegment StartX=-95.0237 StartY=-17.2961 StartZ=0 EndX=-97.0237 EndY=-17.2961 EndZ=0
    g3: LineSegment StartX=-97.0237 StartY=-17.2961 StartZ=0 EndX=-97.0237 EndY=39.7039 EndZ=0
  constraints (11):
    c: Coincident(g0,g1)
    c: Coincident(g1,g2)
    c: Coincident(g3,g0)
    c: Horizontal(g0)
    c: Horizontal(g2)
    c: Vertical(g1)
    c: Vertical(g3)
    c: DistanceX(g0,g0) = 2
    c: Coincident(g3,g2)
    c: DistanceY(g1,g1) = 57
    c: Block(g1)
FEATURE [PartDesign::Pad] Pad038
  Direction = (0,-1,2e-16)
  Length = 56
  Length2 = 10
  Placement = pos=(0,0,0) rot=(1,0,0;1.5708rad)
  Profile = -> Sketch071
  ReferenceAxis = -> Sketch071 [N_Axis]
  Type = 0
FEATURE [Sketcher::SketchObject] Sketch072
  AttachmentOffset = pos=(0,0,-74) rot=(0,0,1;0rad)
  ExternalGeometry = -> [Pad038]
  FullyConstrained = true
  MapMode = 5
  Placement = pos=(-74,1.64e-14,-1.64e-14) rot=(0.57735,0.57735,0.57735;2.0944rad)
  Support = -> [YZ_Plane023]
  sketch-geometry (4):
    g0: LineSegment StartX=-38 StartY=0 StartZ=0 EndX=18 EndY=0 EndZ=0
    g1: LineSegment StartX=18 StartY=0 StartZ=0 EndX=18 EndY=4 EndZ=0
    g2: LineSegment StartX=18 StartY=4 StartZ=0 EndX=-38 EndY=4 EndZ=0
    g3: LineSegment StartX=-38 StartY=4 StartZ=0 EndX=-38 EndY=0 EndZ=0
  constraints (12):
    c: Coincident(g0,g1)
    c: Coincident(g1,g2)
    c: Coincident(g2,g3)
    c: Coincident(g3,g0)
    c: Horizontal(g0)
    c: Horizontal(g2)
    c: Vertical(g1)
    c: Vertical(g3)
    c: PointOnObject(g0,g-3)
    c: PointOnObject(g1,g-4)
    c: PointOnObject(g0,g-1)
    c: DistanceY(g1,g1) = 4
FEATURE [PartDesign::Pad] Pad039
  BaseFeature = -> Pad038
  Direction = (1,-2e-16,3e-16)
  Length = 10
  Length2 = 10
  Placement = pos=(0,0,0) rot=(1,0,0;1.5708rad)
  Profile = -> Sketch072
  ReferenceAxis = -> Sketch072 [N_Axis]
  Type = 3
  UpToFace = -> Pad038 [Face2]
FEATURE [Sketcher::SketchObject] Sketch073
  FullyConstrained = false
  MapMode = 5
  Placement = pos=(0,0,0) rot=(0.57735,0.57735,0.57735;2.0944rad)
  Support = -> [YZ_Plane023]
  sketch-geometry (4):
    g0: LineSegment StartX=-30.4465 StartY=4.63736 StartZ=0 EndX=10.5535 EndY=4.63736 EndZ=0
    g1: LineSegment StartX=10.5535 StartY=4.63736 StartZ=0 EndX=10.5535 EndY=-3.9404 EndZ=0
    g2: LineSegment StartX=10.5535 StartY=-3.9404 StartZ=0 EndX=-30.4465 EndY=-3.9404 EndZ=0
    g3: LineSegment StartX=-30.4465 StartY=-3.9404 StartZ=0 EndX=-30.4465 EndY=4.63736 EndZ=0
  constraints (9):
    c: Coincident(g0,g1)
    c: Coincident(g1,g2)
    c: Coincident(g2,g3)
    c: Coincident(g3,g0)
    c: Horizontal(g0)
    c: Horizontal(g2)
    c: Vertical(g1)
    c: Vertical(g3)
    c: DistanceX(g0,g0) = 41
FEATURE [PartDesign::Pocket] Pocket031
  BaseFeature = -> Pad039
  Direction = (-1,2e-16,-3e-16)
  Length = 0
  Length2 = 5
  Placement = pos=(0,0,0) rot=(1,0,0;1.5708rad)
  Profile = -> Sketch073
  ReferenceAxis = -> Sketch073 [N_Axis]
  Type = 3
  UpToFace = -> Pad039 [Face9]
FEATURE [Sketcher::SketchObject] Sketch074
  FullyConstrained = true
  MapMode = 5
  Support = -> [XY_Plane023]
  sketch-geometry (4):
    g0: Circle CenterX=-88.7181 CenterY=14.6635 CenterZ=0 NormalX=0 NormalY=0 NormalZ=1 AngleXU=0 Radius=1.5
    g1: Circle CenterX=-78.7181 CenterY=14.6635 CenterZ=0 NormalX=0 NormalY=0 NormalZ=1 AngleXU=0 Radius=1.5
    g2: Circle CenterX=-88.7181 CenterY=-34.6965 CenterZ=0 NormalX=0 NormalY=0 NormalZ=1 AngleXU=0 Radius=1.5
    g3: Circle CenterX=-78.7181 CenterY=-34.6965 CenterZ=0 NormalX=0 NormalY=0 NormalZ=1 AngleXU=0 Radius=1.5
  constraints (11):
    c: Equal(g3,g2)
    c: Equal(g3,g1)
    c: Equal(g3,g0)
    c: Diameter(g3) = 3
    c: Horizontal(g0,g1)
    c: DistanceX(g0,g1) = 10
    c: Horizontal(g2,g3)
    c: DistanceX(g2,g3) = 10
    c: Vertical(g2,g0)
    c: Block(g1)
    c: Block(g2)
FEATURE [PartDesign::Pocket] Pocket032
  BaseFeature = -> Pocket031
  Direction = (0,0,-1)
  Length = 5
  Length2 = 5
  Placement = pos=(0,0,0) rot=(1,0,0;1.5708rad)
  Profile = -> Sketch074
  ReferenceAxis = -> Sketch074 [N_Axis]
  Reversed = true
  Type = 1
FEATURE [Sketcher::SketchObject] Sketch075
  AttachmentOffset = pos=(0,0,-1) rot=(0,0,1;0rad)
  FullyConstrained = false
  MapMode = 5
  Placement = pos=(0,1,2e-16) rot=(1,0,0;1.5708rad)
  Support = -> [XZ_Plane022]
  sketch-geometry (4):
    g0: LineSegment StartX=-101.574 StartY=41.4203 StartZ=0 EndX=-97.0564 EndY=41.4203 EndZ=0
    g1: LineSegment StartX=-97.0564 StartY=41.4203 StartZ=0 EndX=-97.0564 EndY=-19.084 EndZ=0
    g2: LineSegment StartX=-97.0564 StartY=-19.084 StartZ=0 EndX=-101.574 EndY=-19.084 EndZ=0
    g3: LineSegment StartX=-101.574 StartY=-19.084 StartZ=0 EndX=-101.574 EndY=41.4203 EndZ=0
  constraints (8):
    c: Coincident(g0,g1)
    c: Coincident(g1,g2)
    c: Coincident(g2,g3)
    c: Coincident(g3,g0)
    c: Horizontal(g0)
    c: Horizontal(g2)
    c: Vertical(g1)
    c: Vertical(g3)
FEATURE [PartDesign::Pocket] Pocket033
  BaseFeature = -> Pocket030
  Direction = (0,1,2e-16)
  Length = 0
  Length2 = 5
  Placement = pos=(0,0,0) rot=(1,0,0;1.5708rad)
  Profile = -> Sketch075
  ReferenceAxis = -> Sketch075 [N_Axis]
  Reversed = true
  Type = 3
  UpToFace = -> Pocket030 [Face17]
FEATURE [PartDesign::Fillet] Fillet018
  Base = -> Pocket033 [Edge57,Edge63,Edge36,Edge51]
  BaseFeature = -> Pocket033
  Placement = pos=(0,0,0) rot=(1,0,0;1.5708rad)
  Radius = 3
  SupportTransform = false
  UseAllEdges = false
FEATURE [Sketcher::SketchObject] Sketch076
  FullyConstrained = true
  MapMode = 5
  Placement = pos=(0,0,0) rot=(0.57735,0.57735,0.57735;2.0944rad)
  Support = -> [YZ_Plane023]
  sketch-geometry (4):
    g0: Circle CenterX=1.41607 CenterY=36.2172 CenterZ=0 NormalX=0 NormalY=0 NormalZ=1 AngleXU=0 Radius=1.5
    g1: Circle CenterX=-8.58393 CenterY=36.2172 CenterZ=0 NormalX=0 NormalY=0 NormalZ=1 AngleXU=0 Radius=1.5
    g2: Circle CenterX=1.41607 CenterY=-13.4772 CenterZ=0 NormalX=0 NormalY=0 NormalZ=1 AngleXU=0 Radius=1.5
    g3: Circle CenterX=-8.58393 CenterY=-13.4772 CenterZ=0 NormalX=0 NormalY=0 NormalZ=1 AngleXU=0 Radius=1.5
  constraints (10):
    c: Equal(g0,g1)
    c: Diameter(g0) = 3
    c: DistanceX(g1,g0) = 10
    c: Horizontal(g0,g1)
    c: Diameter(g3) = 3
    c: Horizontal(g2,g3)
    c: DistanceX(g3,g2) = 10
    c: Vertical(g3,g1)
    c: Block(g1)
    c: Block(g2)
FEATURE [PartDesign::Pocket] Pocket034
  BaseFeature = -> Pocket032
  Direction = (-1,2e-16,-3e-16)
  Length = 0
  Length2 = 5
  Placement = pos=(0,0,0) rot=(1,0,0;1.5708rad)
  Profile = -> Sketch076
  ReferenceAxis = -> Sketch076 [N_Axis]
  Reversed = true
  Type = 3
  UpToFace = -> Fillet018 [Face4]
FEATURE [PartDesign::Fillet] Fillet019
  Base = -> Pocket034 [Edge64,Edge52,Edge54,Edge45]
  BaseFeature = -> Pocket034
  Placement = pos=(0,0,0) rot=(1,0,0;1.5708rad)
  Radius = 3
  SupportTransform = false
  UseAllEdges = false
FEATURE [PartDesign::Fillet] Fillet020
  Base = -> Fillet019 [Edge36,Edge34,Edge45,Edge42]
  BaseFeature = -> Fillet019
  Placement = pos=(0,0,0) rot=(1,0,0;1.5708rad)
  Radius = 10
  SupportTransform = false
  UseAllEdges = false
FEATURE [PartDesign::Body] Body023  label="coxa_008"
  Group = -> [Sketch071,Pad038,Sketch072,Pad039,Sketch073,Pocket031,Sketch074,Pocket032,Sketch076,Pocket034,Fillet019,Fillet020]
  Origin = -> Origin023
  Placement = pos=(0,20.26,0) rot=(0,0,1;0rad)
  Tip = -> Fillet020
FEATURE [Sketcher::SketchObject] Sketch077
  FullyConstrained = true
  MapMode = 5
  Placement = pos=(0,0,0) rot=(0.57735,0.57735,0.57735;2.0944rad)
  Support = -> [YZ_Plane022]
  sketch-geometry (4):
    g0: Circle CenterX=-21.1481 CenterY=35.969 CenterZ=0 NormalX=0 NormalY=0 NormalZ=1 AngleXU=0 Radius=1.5
    g1: Circle CenterX=-11.1481 CenterY=35.969 CenterZ=0 NormalX=0 NormalY=0 NormalZ=1 AngleXU=0 Radius=1.5
    g2: Circle CenterX=-21.1481 CenterY=-13.7095 CenterZ=0 NormalX=0 NormalY=0 NormalZ=1 AngleXU=0 Radius=1.5
    g3: Circle CenterX=-11.1481 CenterY=-13.7095 CenterZ=0 NormalX=0 NormalY=0 NormalZ=1 AngleXU=0 Radius=1.5
  constraints (11):
    c: Equal(g3,g2)
    c: Equal(g3,g0)
    c: Equal(g3,g1)
    c: Diameter(g3) = 3
    c: Horizontal(g0,g1)
    c: DistanceX(g0,g1) = 10
    c: Horizontal(g2,g3)
    c: DistanceX(g2,g3) = 10
    c: Vertical(g2,g0)
    c: Block(g1)
    c: Block(g2)
FEATURE [PartDesign::Pocket] Pocket035
  BaseFeature = -> Fillet018
  Direction = (-1,2e-16,-3e-16)
  Length = 0
  Length2 = 5
  Placement = pos=(0,0,0) rot=(1,0,0;1.5708rad)
  Profile = -> Sketch077
  ReferenceAxis = -> Sketch077 [N_Axis]
  Type = 3
  UpToFace = -> Fillet018 [Face4]
FEATURE [PartDesign::Body] Body022  label="coxa_007"
  Group = -> [Sketch067,Pad036,Sketch068,Pad037,Sketch069,Pocket029,Sketch070,Pocket030,Sketch075,Pocket033,Fillet018,Sketch077,Pocket035]
  Origin = -> Origin022
  Placement = pos=(0,0.648711,22.5479) rot=(1,0,0;3.1381rad)
  Tip = -> Pocket035
FEATURE [App::LinkGroup] LinkGroup017  label="LegBR"
  ElementList = -> [Body020,LinkGroup016,LinkGroup015,LinkGroup014,Body022,Body023,Body021]
  LinkMode = 0
  Placement = pos=(-294.93,0.98991,150.58) rot=(0,0,1;3.1381rad)
FEATURE [Sketcher::SketchObject] Sketch
  FullyConstrained = true
  MapMode = 5
  Placement = pos=(0,0,0) rot=(1,0,0;1.5708rad)
  Support = -> [XZ_Plane]
  sketch-geometry (13):
    g0: ArcOfCircle CenterX=-36.4422 CenterY=66.0924 CenterZ=0 NormalX=0 NormalY=0 NormalZ=1 AngleXU=0 Radius=10.6677 StartAngle=1.5708 EndAngle=4.71239
    g1: ArcOfCircle CenterX=33.5578 CenterY=66.0924 CenterZ=0 NormalX=0 NormalY=0 NormalZ=1 AngleXU=0 Radius=10.6677 StartAngle=4.71239 EndAngle=7.85398
    g2: LineSegment StartX=-36.4422 StartY=55.4247 StartZ=0 EndX=33.5578 EndY=55.4247 EndZ=0
    g3: LineSegment StartX=33.5578 StartY=76.7601 StartZ=0 EndX=-36.4422 EndY=76.7601 EndZ=0
    g4: Circle CenterX=-36.4422 CenterY=73.0825 CenterZ=0 NormalX=0 NormalY=0 NormalZ=1 AngleXU=0 Radius=1.2926
    g5: Circle CenterX=-29.4478 CenterY=66.0924 CenterZ=0 NormalX=0 NormalY=0 NormalZ=1 AngleXU=0 Radius=1.2926
    g6: Circle CenterX=-43.4478 CenterY=66.0924 CenterZ=0 NormalX=0 NormalY=0 NormalZ=1 AngleXU=0 Radius=1.2926
    g7: Circle CenterX=-36.4422 CenterY=59.0825 CenterZ=0 NormalX=0 NormalY=0 NormalZ=1 AngleXU=0 Radius=1.2926
    g8: Circle CenterX=33.5578 CenterY=66.0924 CenterZ=0 NormalX=0 NormalY=0 NormalZ=1 AngleXU=0 Radius=1.5
    g9: Circle CenterX=33.5578 CenterY=73.0825 CenterZ=0 NormalX=0 NormalY=0 NormalZ=1 AngleXU=0 Radius=1.5
    g10: Circle CenterX=33.5578 CenterY=59.0825 CenterZ=0 NormalX=0 NormalY=0 NormalZ=1 AngleXU=0 Radius=1.5
    g11: Circle CenterX=40.5578 CenterY=66.0924 CenterZ=0 NormalX=0 NormalY=0 NormalZ=1 AngleXU=0 Radius=1.5
    g12: Circle CenterX=26.5578 CenterY=66.0924 CenterZ=0 NormalX=0 NormalY=0 NormalZ=1 AngleXU=0 Radius=1.5
  constraints (33):
    c: Tangent(g0,g2) = -1.5708
    c: Tangent(g2,g1) = -1.5708
    c: Tangent(g1,g3) = -1.5708
    c: Tangent(g3,g0) = -1.5708
    c: Equal(g0,g1)
    c: Horizontal(g2)
    c: Block(g0)
    c: Equal(g6,g4)
    c: Equal(g4,g5)
    c: Equal(g5,g7)
    c: Vertical(g4,g0)
    c: Vertical(g0,g7)
    c: Horizontal(g6,g0)
    c: Horizontal(g0,g5)
    c: DistanceX(g6,g5) = 14
    c: DistanceY(g7,g4) = 14
    c: Block(g4)
    c: Block(g6)
    c: Coincident(g8,g1)
    c: Equal(g8,g9)
    c: Equal(g8,g10)
    c: Equal(g8,g12)
    c: Equal(g8,g11)
    c: Diameter(g8) = 3
    c: Horizontal(g12,g1)
    c: Horizontal(g1,g11)
    c: Vertical(g9,g10)
    c: Vertical(g10,g1)
    c: Horizontal(g9,g4)
    c: DistanceX(g12,g11) = 14
    c: DistanceY(g10,g9) = 14
    c: DistanceX(g7,g10) = 70
    c: DistanceX(g1,g11) = 7
FEATURE [App::MeasureDistance] Distance  label="Distance: 108.26 mm"
  Distance = 108.262
  P1 = (-10.0774,-0.0705017,-12.16)
  P2 = (97.4998,2.42045e-11,0)
FEATURE [App::MeasureDistance] Distance001  label="Distance: 73.58 mm"
  Distance = 73.5767
  P1 = (-83.6427,-0.253448,-12.16)
  P2 = (-10.066,-0.253441,-12.16)
FEATURE [App::MeasureDistance] Distance002  label="Distance: 27.41 mm"
  Distance = 27.4072
  P1 = (-83.5195,-0.482428,-12.16)
  P2 = (-110.728,-0.647339,-15.4466)
FEATURE [Part::Part2DObjectPython] Circle  # Draft 2D object (typed FeaturePython)
  Area = 3.12379
  FirstAngle = 0
  LastAngle = 0
  MakeFace = true
  Placement = pos=(-184.438,1.14014e-05,152.087) rot=(0,0.707107,0.707107;3.14159rad)
  Radius = 0.997163
FEATURE [Part::Part2DObjectPython] Rectangle  # Draft 2D object (typed FeaturePython)
  Area = 1.91216
  ChamferSize = 0
  Columns = 1
  FilletRadius = 0
  Height = 1.59471
  Length = 1.19907
  MakeFace = true
  Placement = pos=(-183.842,1.13646e-05,151.292) rot=(0,0.707107,0.707107;3.14159rad)
  Rows = 1
FEATURE [Part::Part2DObjectPython] Line  # Draft 2D object (typed FeaturePython)
  Area = 0
  ChamferSize = 0
  Closed = false
  End = (-183.845,1.13648e-05,151.292)
  FilletRadius = 0
  Length = 1.99763
  MakeFace = true
  Placement = pos=(-185.044,1.14389e-05,152.889) rot=(0,0.707107,0.707107;3.14159rad)
  Points = (2) [(0,0,0),(-1.19907,-1.59773,4.15018e-15)]
  Start = (-185.044,1.14389e-05,152.889)
  Subdivisions = 0
FEATURE [Part::Part2DObjectPython] Line001  # Draft 2D object (typed FeaturePython)
  Area = 0
  ChamferSize = 0
  Closed = false
  End = (-185.044,1.14389e-05,151.289)
  FilletRadius = 0
  Length = 1.99581
  MakeFace = true
  Placement = pos=(-183.848,1.1365e-05,152.886) rot=(0,0.707107,0.707107;3.14159rad)
  Points = (2) [(0,0,0),(1.19605,-1.59773,2.58069e-15)]
  Start = (-183.848,1.1365e-05,152.886)
  Subdivisions = 0
FEATURE [Part::FeaturePython] Point  # WARN: FeaturePython — macro-defined, semantics opaque (R4)
  Placement = pos=(-184.443,1.14018e-05,152.089) rot=(0,0,1;0rad)
  X = -184.443
  Y = 1.14018e-05
  Z = 152.089
FEATURE [PartDesign::Pad] Pad
  Direction = (0,-1,-2e-16)
  Length = 8
  Length2 = 10
  Placement = pos=(0,0,0) rot=(1,0,0;1.5708rad)
  Profile = -> Sketch
  ReferenceAxis = -> Sketch [N_Axis]
  Reversed = true
  Type = 0
FEATURE [PartDesign::Body] Body  label="temp"
  Group = -> [Sketch,Pad]
  Origin = -> Origin
  Placement = pos=(-148,0,86) rot=(0,0,1;0rad)
  Tip = -> Pad
FEATURE [App::DocumentObjectGroup] Group006  label="misc"
  Group = -> [Body,Distance,Distance001,Distance002,Circle,Rectangle,Line,Line001,Point]
FEATURE [Sketcher::SketchObject] Sketch078
  FullyConstrained = true
  MapMode = 5
  Placement = pos=(0,0,0) rot=(1,0,0;1.5708rad)
  Support = -> [XZ_Plane024]
  sketch-geometry (36):
    g0: ArcOfCircle CenterX=-184.442 CenterY=72.0892 CenterZ=0 NormalX=0 NormalY=0 NormalZ=1 AngleXU=0 Radius=10.5 StartAngle=1.5708 EndAngle=4.71239
    g1: ArcOfCircle CenterX=-104.442 CenterY=72.0892 CenterZ=0 NormalX=0 NormalY=0 NormalZ=1 AngleXU=0 Radius=10.5 StartAngle=4.71239 EndAngle=7.85398
    g2: LineSegment StartX=-184.442 StartY=61.5892 StartZ=0 EndX=-104.442 EndY=61.5892 EndZ=0
    g3: LineSegment StartX=-104.442 StartY=82.5892 StartZ=0 EndX=-124.442 EndY=82.5892 EndZ=0
    g4: ArcOfCircle CenterX=-184.442 CenterY=152.089 CenterZ=0 NormalX=0 NormalY=0 NormalZ=1 AngleXU=0 Radius=10.5 StartAngle=1.5708 EndAngle=4.71239
    g5: ArcOfCircle CenterX=-104.442 CenterY=152.089 CenterZ=0 NormalX=0 NormalY=0 NormalZ=1 AngleXU=0 Radius=10.5 StartAngle=4.71239 EndAngle=7.85398
    g6: LineSegment StartX=-184.442 StartY=141.589 StartZ=0 EndX=-164.442 EndY=141.589 EndZ=0
    g7: LineSegment StartX=-104.442 StartY=162.589 StartZ=0 EndX=-184.442 EndY=162.589 EndZ=0
    g8: LineSegment StartX=-124.442 StartY=82.5892 StartZ=0 EndX=-124.442 EndY=141.589 EndZ=0
    g9: LineSegment StartX=-164.442 StartY=141.589 StartZ=0 EndX=-164.442 EndY=82.5892 EndZ=0
    g10: Circle CenterX=-184.442 CenterY=65.0892 CenterZ=0 NormalX=0 NormalY=0 NormalZ=1 AngleXU=0 Radius=1.5
    g11: Circle CenterX=-177.442 CenterY=72.0892 CenterZ=0 NormalX=0 NormalY=0 NormalZ=1 AngleXU=0 Radius=1.5
    g12: Circle CenterX=-191.442 CenterY=72.0892 CenterZ=0 NormalX=0 NormalY=0 NormalZ=1 AngleXU=0 Radius=1.5
    g13: Circle CenterX=-184.442 CenterY=79.0892 CenterZ=0 NormalX=0 NormalY=0 NormalZ=1 AngleXU=0 Radius=1.5
    g14: Circle CenterX=-104.442 CenterY=65.0892 CenterZ=0 NormalX=0 NormalY=0 NormalZ=1 AngleXU=0 Radius=1.5
    g15: Circle CenterX=-97.4423 CenterY=72.0892 CenterZ=0 NormalX=0 NormalY=0 NormalZ=1 AngleXU=0 Radius=1.5
    g16: Circle CenterX=-104.442 CenterY=79.0892 CenterZ=0 NormalX=0 NormalY=0 NormalZ=1 AngleXU=0 Radius=1.5
    g17: Circle CenterX=-111.442 CenterY=72.0892 CenterZ=0 NormalX=0 NormalY=0 NormalZ=1 AngleXU=0 Radius=1.5
    g18: Circle CenterX=-104.442 CenterY=145.089 CenterZ=0 NormalX=0 NormalY=0 NormalZ=1 AngleXU=0 Radius=1.5
    g19: Circle CenterX=-97.4423 CenterY=152.089 CenterZ=0 NormalX=0 NormalY=0 NormalZ=1 AngleXU=0 Radius=1.5
    g20: Circle CenterX=-111.442 CenterY=152.089 CenterZ=0 NormalX=0 NormalY=0 NormalZ=1 AngleXU=0 Radius=1.5
    g21: Circle CenterX=-104.442 CenterY=159.089 CenterZ=0 NormalX=0 NormalY=0 NormalZ=1 AngleXU=0 Radius=1.5
    g22: Circle CenterX=-184.442 CenterY=145.089 CenterZ=0 NormalX=0 NormalY=0 NormalZ=1 AngleXU=0 Radius=1.5
    g23: Circle CenterX=-191.442 CenterY=152.089 CenterZ=0 NormalX=0 NormalY=0 NormalZ=1 AngleXU=0 Radius=1.5
    g24: Circle CenterX=-177.442 CenterY=152.089 CenterZ=0 NormalX=0 NormalY=0 NormalZ=1 AngleXU=0 Radius=1.5
    g25: Circle CenterX=-184.442 CenterY=159.089 CenterZ=0 NormalX=0 NormalY=0 NormalZ=1 AngleXU=0 Radius=1.5
    g26: Circle CenterX=-184.442 CenterY=152.089 CenterZ=0 NormalX=0 NormalY=0 NormalZ=1 AngleXU=0 Radius=1.5
    g27: Circle CenterX=-104.442 CenterY=152.089 CenterZ=0 NormalX=0 NormalY=0 NormalZ=1 AngleXU=0 Radius=1.5
    g28: Circle CenterX=-184.442 CenterY=72.0892 CenterZ=0 NormalX=0 NormalY=0 NormalZ=1 AngleXU=0 Radius=1.5
    g29: Circle CenterX=-104.442 CenterY=72.0892 CenterZ=0 NormalX=0 NormalY=0 NormalZ=1 AngleXU=0 Radius=1.5
    g30: LineSegment StartX=-124.442 StartY=141.589 StartZ=0 EndX=-104.442 EndY=141.589 EndZ=0
    g31: LineSegment StartX=-164.442 StartY=82.5892 StartZ=0 EndX=-184.442 EndY=82.5892 EndZ=0
    g32: Circle CenterX=-154.442 CenterY=151.589 CenterZ=0 NormalX=0 NormalY=0 NormalZ=1 AngleXU=0 Radius=1.5
    g33: Circle CenterX=-134.442 CenterY=151.589 CenterZ=0 NormalX=0 NormalY=0 NormalZ=1 AngleXU=0 Radius=1.5
    g34: Circle CenterX=-154.442 CenterY=72.5892 CenterZ=0 NormalX=0 NormalY=0 NormalZ=1 AngleXU=0 Radius=1.5
    g35: Circle CenterX=-134.442 CenterY=72.5892 CenterZ=0 NormalX=0 NormalY=0 NormalZ=1 AngleXU=0 Radius=1.5
  constraints (95):
    c: Tangent(g0,g2) = -1.5708
    c: Tangent(g2,g1) = -1.5708
    c: Tangent(g1,g3) = -1.5708
    c: Coincident(g31,g0) = -1.5708
    c: Equal(g0,g1)
    c: Horizontal(g2)
    c: Tangent(g4,g6) = -1.5708
    c: Coincident(g30,g5) = -1.5708
    c: Tangent(g5,g7) = -1.5708
    c: Tangent(g7,g4) = -1.5708
    c: Equal(g4,g5)
    c: Horizontal(g6)
    c: DistanceY(g0,g0) = 21
    c: DistanceX(g0,g1) = 80
    c: Equal(g0,g4)
    c: Vertical(g4,g0)
    c: Block(g4)
    c: DistanceY(g0,g4) = 80
    c: Vertical(g8)
    c: Vertical(g9)
    c: DistanceX(g9,g8) = 40
    c: DistanceX(g4,g9) = 20
    c: Equal(g23,g22)
    c: Equal(g23,g24)
    c: Equal(g23,g25)
    c: Equal(g23, g18-g21) x4
    c: Equal(g23,g14)
    c: Equal(g23,g17)
    c: Equal(g23,g16)
    c: Equal(g23,g15)
    c: Equal(g23, g10-g13) x4
    c: Diameter(g23) = 3
    c: Vertical(g10,g0)
    c: Vertical(g0,g13)
    c: Vertical(g13,g22)
    c: Vertical(g4,g25)
    c: Coincident(g26,g4)
    c: Diameter(g26) = 3
    c: DistanceY(g22,g25) = 14
    c: DistanceY(g22,g4) = 7
    c: Horizontal(g23,g4)
    c: Horizontal(g4,g24)
    c: Horizontal(g24,g20)
    c: Horizontal(g20,g19)
    c: Vertical(g5,g18)
    c: Vertical(g18,g21)
    c: DistanceY(g18,g21) = 14
    c: Horizontal(g18,g22)
    c: DistanceX(g20,g19) = 14
    c: DistanceX(g20,g5) = 7
    c: Vertical(g1,g16)
    c: Vertical(g16,g14)
    c: Horizontal(g17,g1)
    c: Horizontal(g1,g15)
    c: DistanceY(g14,g16) = 14
    c: DistanceY(g1,g16) = 7
    c: DistanceX(g17,g15) = 14
    c: DistanceX(g17,g1) = 7
    c: DistanceY(g10,g13) = 14
    c: DistanceY(g0,g13) = 7
    c: DistanceX(g12,g11) = 14
    c: DistanceX(g0,g11) = 7
    c: Horizontal(g12,g0)
    c: Horizontal(g0,g11)
    c: Coincident(g27,g5)
    c: Equal(g27,g19)
    c: DistanceX(g23,g4) = 7
    c: DistanceX(g4,g24) = 7
    c: Coincident(g28,g0)
    c: Coincident(g29,g1)
    c: Equal(g29,g28)
    c: Equal(g28,g11)
    c: Coincident(g30,g8)
    c: Equal(g8,g9)
    c: Block(g8)
    c: Block(g7)
    c: Block(g5)
    c: Block(g6)
    c: Block(g9)
    c: Block(g31)
    c: Block(g3)
    c: DistanceY(g9,g6) = 59
    c: DistanceY(g6,g4) = 21
    c: Equal(g35,g34)
    c: Equal(g35,g33)
    c: Equal(g35,g32)
    c: Diameter(g35) = 3
    c: Vertical(g32,g34)
    c: Vertical(g33,g35)
    c: Horizontal(g34,g35)
    c: DistanceX(g34,g35) = 20
    c: Horizontal(g33,g32)
    c: DistanceX(g9,g34) = 10
    c: DistanceY(g34,g9) = 10
    c: DistanceY(g6,g32) = 10
FEATURE [Mesh::Feature] ESP32_WROOM_32  label="ESP32-WROOM-32"
  Placement = pos=(-121.375,39.305,131.479) rot=(0.580196,-0.577886,-0.573951;4.18597rad)
FEATURE [Mesh::Feature] PCA9685_v18  label="PCA9685 v18"
  Placement = pos=(-151.474,26.0281,142.302) rot=(-0.57614,0.577753,0.578155;2.0944rad)
FEATURE [App::DocumentObjectGroup] Group  label="commons"
  Group = -> [PCA9685_v18,MG996,MG997,MG955_horn___Part_002,MG955_horn___Part_1,_98zz_Bearing,ESP32_WROOM_32]
FEATURE [PartDesign::Pad] Pad040
  Direction = (0,-1,2e-16)
  Length = 5
  Length2 = 10
  Placement = pos=(0,0,0) rot=(1,0,0;1.5708rad)
  Profile = -> Sketch078
  ReferenceAxis = -> Sketch078 [N_Axis]
  Type = 0
FEATURE [Sketcher::SketchObject] Sketch079
  FullyConstrained = false
  MapMode = 5
  Placement = pos=(0,0,0) rot=(1,0,0;1.5708rad)
  Support = -> [XZ_Plane024]
  sketch-geometry (4):
    g0: LineSegment StartX=-149.719 StartY=144.764 StartZ=0 EndX=-139.719 EndY=144.764 EndZ=0
    g1: LineSegment StartX=-139.719 StartY=144.764 StartZ=0 EndX=-139.719 EndY=79.7642 EndZ=0
    g2: LineSegment StartX=-139.719 StartY=79.7642 StartZ=0 EndX=-149.719 EndY=79.7642 EndZ=0
    g3: LineSegment StartX=-149.719 StartY=79.7642 StartZ=0 EndX=-149.719 EndY=144.764 EndZ=0
  constraints (10):
    c: Coincident(g0,g1)
    c: Coincident(g1,g2)
    c: Coincident(g2,g3)
    c: Coincident(g3,g0)
    c: Horizontal(g0)
    c: Horizontal(g2)
    c: Vertical(g1)
    c: Vertical(g3)
    c: DistanceX(g0,g0) = 10
    c: DistanceY(g1,g1) = 65
FEATURE [PartDesign::Pad] Pad041
  BaseFeature = -> Pad040
  Direction = (0,-1,2e-16)
  Length = 35
  Length2 = 10
  Placement = pos=(0,0,0) rot=(1,0,0;1.5708rad)
  Profile = -> Sketch079
  ReferenceAxis = -> Sketch079 [N_Axis]
  Reversed = true
  Type = 0
FEATURE [Sketcher::SketchObject] Sketch080
  FullyConstrained = true
  MapMode = 5
  Placement = pos=(0,0,0) rot=(0.57735,0.57735,0.57735;2.0944rad)
  Support = -> [YZ_Plane024]
  sketch-geometry (8):
    g0: Circle CenterX=26.3071 CenterY=140.582 CenterZ=0 NormalX=0 NormalY=0 NormalZ=1 AngleXU=0 Radius=1.5
    g1: Circle CenterX=26.3071 CenterY=84.5821 CenterZ=0 NormalX=0 NormalY=0 NormalZ=1 AngleXU=0 Radius=1.5
    g2: Circle CenterX=7.30708 CenterY=84.5821 CenterZ=0 NormalX=0 NormalY=0 NormalZ=1 AngleXU=0 Radius=1.5
    g3: Circle CenterX=7.30708 CenterY=140.582 CenterZ=0 NormalX=0 NormalY=0 NormalZ=1 AngleXU=0 Radius=1.5
    g4: Circle CenterX=26.3071 CenterY=135.582 CenterZ=0 NormalX=0 NormalY=0 NormalZ=1 AngleXU=0 Radius=1.5
    g5: Circle CenterX=2.80708 CenterY=135.582 CenterZ=0 NormalX=0 NormalY=0 NormalZ=1 AngleXU=0 Radius=1.5
    g6: Circle CenterX=26.3071 CenterY=89.5821 CenterZ=0 NormalX=0 NormalY=0 NormalZ=1 AngleXU=0 Radius=1.5
    g7: Circle CenterX=2.80708 CenterY=89.5821 CenterZ=0 NormalX=0 NormalY=0 NormalZ=1 AngleXU=0 Radius=1.5
  constraints (25):
    c: Diameter(g0) = 3
    c: Block(g0)
    c: Equal(g3,g0)
    c: Equal(g0,g1)
    c: Equal(g1,g2)
    c: Vertical(g0,g1)
    c: Block(g1)
    c: Horizontal(g1,g2)
    c: Block(g2)
    c: Vertical(g2,g3)
    c: Horizontal(g3,g0)
    c: Equal(g6,g7)
    c: Equal(g7,g4)
    c: Equal(g4,g5)
    c: Equal(g5,g3)
    c: Horizontal(g4,g5)
    c: DistanceX(g5,g4) = 23.5
    c: DistanceX(g3,g0) = 19
    c: DistanceY(g2,g3) = 56
    c: Horizontal(g7,g6)
    c: Vertical(g6,g4)
    c: DistanceY(g6,g4) = 46
    c: Vertical(g6,g1)
    c: Vertical(g7,g5)
    c: DistanceY(g4,g0) = 5
FEATURE [PartDesign::Pocket] Pocket036
  BaseFeature = -> Pad041
  Direction = (-1,2e-16,-3e-16)
  Length = 5
  Length2 = 5
  Midplane = true
  Placement = pos=(0,0,0) rot=(1,0,0;1.5708rad)
  Profile = -> Sketch080
  ReferenceAxis = -> Sketch080 [N_Axis]
  Type = 1
FEATURE [PartDesign::Pad] Pad008
  Direction = (0,0,1)
  Length = 3
  Length2 = 10
  Profile = -> Sketch011
  ReferenceAxis = -> Sketch011 [N_Axis]
  Type = 0
FEATURE [PartDesign::Pocket] Pocket
  BaseFeature = -> Pad008
  Direction = (0,0,-1)
  Length = 3
  Length2 = 5
  Profile = -> Sketch013
  ReferenceAxis = -> Sketch013 [N_Axis]
  Reversed = true
  Type = 0
FEATURE [PartDesign::Body] Body001  label="femur_x"
  Group = -> [Sketch011,Pad008,Sketch013,Pocket]
  Origin = -> Origin001
  Placement = pos=(0,0,-19) rot=(0,0,1;0rad)
  Tip = -> Pocket
FEATURE [App::DocumentObjectGroup] Group001  label="femur"
  Group = -> [Body001]
FEATURE [App::LinkGroup] LinkGroup005  label="LegFL"
  ElementList = -> [Body001,LinkGroup004,LinkGroup003,LinkGroup,Body009,Body010,Body008]
  LinkMode = 0
  Placement = pos=(5.57,-6.67572e-06,50.54) rot=(0,0,1;0rad)
FEATURE [App::DocumentObjectGroup] Group005  label="Legs"
  Group = -> [LinkGroup005,LinkGroup009,LinkGroup013,LinkGroup017]
FEATURE [PartDesign::Fillet] Fillet
  Base = -> Pocket036 [Edge86,Edge84,Edge81,Edge114,Edge102,Edge5,Edge33,Edge31]
  BaseFeature = -> Pocket036
  Placement = pos=(0,0,0) rot=(1,0,0;1.5708rad)
  Radius = 10
  SupportTransform = false
  UseAllEdges = false
FEATURE [PartDesign::Body] Body024  label="quadraped body"
  Group = -> [Sketch078,Pad040,Sketch079,Pad041,Sketch080,Pocket036,Fillet]
  Origin = -> Origin024
  Placement = pos=(0,21.23,0) rot=(0,0,1;0rad)
  Tip = -> Fillet
FEATURE [Part::FeaturePython] InvoluteGear  # WARN: FeaturePython — macro-defined, semantics opaque (R4)
  AttacherType = Attacher::AttachEngine3D
  addendum_diameter = 29
  angular_backlash = 0
  axle_hole = false
  axle_holesize = 10
  backlash = 0
  clearance = 0.25
  double_helix = false
  head = 0
  head_fillet = 0
  height = 6
  helix_angle = 0
  module = 1
  num_teeth = 27
  numpoints = 45
  offset_hole = false
  offset_holeoffset = 10
  offset_holesize = 10
  pitch_diameter = 27
  pressure_angle = 20
  properties_from_tool = false
  reversed_backlash = false
  root_diameter = 24.5
  root_fillet = 0
  shift = 0
  simple = false
  transverse_pitch = 3.14159
  traverse_module = 1
  undercut = false
  version = 1.3.0
  expr: angular_backlash = backlash / pitch_diameter * 360 ° / pi
FEATURE [Part::FeaturePython] InternalInvoluteGear  # WARN: FeaturePython — macro-defined, semantics opaque (R4)
  AttacherType = Attacher::AttachEngine3D
  Placement = pos=(-30.36,-50.31,0) rot=(0,0,1;0rad)
  addendum_diameter = 13.8
  angular_backlash = 0
  backlash = 0
  clearance = 0.25
  double_helix = false
  head = -0.4
  head_fillet = 0
  height = 5
  helix_angle = 0
  module = 1
  num_teeth = 15
  numpoints = 20
  outside_diameter = 25
  pitch_diameter = 15
  pressure_angle = 20
  properties_from_tool = false
  reversed_backlash = false
  root_diameter = 17.5
  root_fillet = 0
  shift = 0
  simple = false
  thickness = 5
  transverse_pitch = 3.14159
  version = 1.3.0
  expr: angular_backlash = backlash / pitch_diameter * 360 ° / pi
